FCSTD DOCUMENT  (FreeCAD 1.0R38641 +468 (Git))
Label: freecadCase
License: All rights reserved
LicenseURL: https://en.wikipedia.org/wiki/All_rights_reserved
objects: Sketcher::SketchObject×2, PartDesign::Body×1
note: 5 computed .brp shape members not serialized (recipe doc carries the construction recipe); baked Part::Feature solids carry a one-line shape summary decoded from their .brp

FEATURE [Sketcher::SketchObject] Sketch
  ArcFitTolerance = 1e-06
  FullyConstrained = false
  MakeInternals = false
  sketch-geometry (816):
    g0: LineSegment StartX=3.025 StartY=-2.525 StartZ=0 EndX=16.025 EndY=-2.525 EndZ=0
    g1: LineSegment StartX=3.025 StartY=-16.525 StartZ=0 EndX=16.025 EndY=-16.525 EndZ=0
    g2: LineSegment StartX=2.525 StartY=-3.025 StartZ=0 EndX=2.525 EndY=-16.025 EndZ=0
    g3: LineSegment StartX=16.525 StartY=-3.025 StartZ=0 EndX=16.525 EndY=-16.025 EndZ=0
    g4: ArcOfCircle CenterX=3.025 CenterY=-3.025 CenterZ=0 NormalX=0 NormalY=0 NormalZ=1 AngleXU=0 Radius=0.5 StartAngle=1.5708 EndAngle=3.14159
    g5: ArcOfCircle CenterX=16.025 CenterY=-3.025 CenterZ=0 NormalX=0 NormalY=0 NormalZ=1 AngleXU=0 Radius=0.5 StartAngle=0 EndAngle=1.5708
    g6: ArcOfCircle CenterX=3.025 CenterY=-16.025 CenterZ=0 NormalX=0 NormalY=0 NormalZ=1 AngleXU=0 Radius=0.5 StartAngle=3.14159 EndAngle=4.71239
    g7: ArcOfCircle CenterX=16.025 CenterY=-16.025 CenterZ=0 NormalX=0 NormalY=0 NormalZ=1 AngleXU=0 Radius=0.5 StartAngle=4.71239 EndAngle=6.28319
    g8: LineSegment StartX=22.075 StartY=-2.525 StartZ=0 EndX=35.075 EndY=-2.525 EndZ=0
    g9: LineSegment StartX=22.075 StartY=-16.525 StartZ=0 EndX=35.075 EndY=-16.525 EndZ=0
    g10: LineSegment StartX=21.575 StartY=-3.025 StartZ=0 EndX=21.575 EndY=-16.025 EndZ=0
    g11: LineSegment StartX=35.575 StartY=-3.025 StartZ=0 EndX=35.575 EndY=-16.025 EndZ=0
    g12: ArcOfCircle CenterX=22.075 CenterY=-3.025 CenterZ=0 NormalX=0 NormalY=0 NormalZ=1 AngleXU=0 Radius=0.5 StartAngle=1.5708 EndAngle=3.14159
    g13: ArcOfCircle CenterX=35.075 CenterY=-3.025 CenterZ=0 NormalX=0 NormalY=0 NormalZ=1 AngleXU=0 Radius=0.5 StartAngle=0 EndAngle=1.5708
    g14: ArcOfCircle CenterX=22.075 CenterY=-16.025 CenterZ=0 NormalX=0 NormalY=0 NormalZ=1 AngleXU=0 Radius=0.5 StartAngle=3.14159 EndAngle=4.71239
    g15: ArcOfCircle CenterX=35.075 CenterY=-16.025 CenterZ=0 NormalX=0 NormalY=0 NormalZ=1 AngleXU=0 Radius=0.5 StartAngle=4.71239 EndAngle=6.28319
    g16: LineSegment StartX=41.125 StartY=-2.525 StartZ=0 EndX=54.125 EndY=-2.525 EndZ=0
    g17: LineSegment StartX=41.125 StartY=-16.525 StartZ=0 EndX=54.125 EndY=-16.525 EndZ=0
    g18: LineSegment StartX=40.625 StartY=-3.025 StartZ=0 EndX=40.625 EndY=-16.025 EndZ=0
    g19: LineSegment StartX=54.625 StartY=-3.025 StartZ=0 EndX=54.625 EndY=-16.025 EndZ=0
    g20: ArcOfCircle CenterX=41.125 CenterY=-3.025 CenterZ=0 NormalX=0 NormalY=0 NormalZ=1 AngleXU=0 Radius=0.5 StartAngle=1.5708 EndAngle=3.14159
    g21: ArcOfCircle CenterX=54.125 CenterY=-3.025 CenterZ=0 NormalX=0 NormalY=0 NormalZ=1 AngleXU=0 Radius=0.5 StartAngle=0 EndAngle=1.5708
    g22: ArcOfCircle CenterX=41.125 CenterY=-16.025 CenterZ=0 NormalX=0 NormalY=0 NormalZ=1 AngleXU=0 Radius=0.5 StartAngle=3.14159 EndAngle=4.71239
    g23: ArcOfCircle CenterX=54.125 CenterY=-16.025 CenterZ=0 NormalX=0 NormalY=0 NormalZ=1 AngleXU=0 Radius=0.5 StartAngle=4.71239 EndAngle=6.28319
    g24: LineSegment StartX=60.175 StartY=-2.525 StartZ=0 EndX=73.175 EndY=-2.525 EndZ=0
    g25: LineSegment StartX=60.175 StartY=-16.525 StartZ=0 EndX=73.175 EndY=-16.525 EndZ=0
    g26: LineSegment StartX=59.675 StartY=-3.025 StartZ=0 EndX=59.675 EndY=-16.025 EndZ=0
    g27: LineSegment StartX=73.675 StartY=-3.025 StartZ=0 EndX=73.675 EndY=-16.025 EndZ=0
    g28: ArcOfCircle CenterX=60.175 CenterY=-3.025 CenterZ=0 NormalX=0 NormalY=0 NormalZ=1 AngleXU=0 Radius=0.5 StartAngle=1.5708 EndAngle=3.14159
    g29: ArcOfCircle CenterX=73.175 CenterY=-3.025 CenterZ=0 NormalX=0 NormalY=0 NormalZ=1 AngleXU=0 Radius=0.5 StartAngle=0 EndAngle=1.5708
    g30: ArcOfCircle CenterX=60.175 CenterY=-16.025 CenterZ=0 NormalX=0 NormalY=0 NormalZ=1 AngleXU=0 Radius=0.5 StartAngle=3.14159 EndAngle=4.71239
    g31: ArcOfCircle CenterX=73.175 CenterY=-16.025 CenterZ=0 NormalX=0 NormalY=0 NormalZ=1 AngleXU=0 Radius=0.5 StartAngle=4.71239 EndAngle=6.28319
    g32: LineSegment StartX=79.225 StartY=-2.525 StartZ=0 EndX=92.225 EndY=-2.525 EndZ=0
    g33: LineSegment StartX=79.225 StartY=-16.525 StartZ=0 EndX=92.225 EndY=-16.525 EndZ=0
    g34: LineSegment StartX=78.725 StartY=-3.025 StartZ=0 EndX=78.725 EndY=-16.025 EndZ=0
    g35: LineSegment StartX=92.725 StartY=-3.025 StartZ=0 EndX=92.725 EndY=-16.025 EndZ=0
    g36: ArcOfCircle CenterX=79.225 CenterY=-3.025 CenterZ=0 NormalX=0 NormalY=0 NormalZ=1 AngleXU=0 Radius=0.5 StartAngle=1.5708 EndAngle=3.14159
    g37: ArcOfCircle CenterX=92.225 CenterY=-3.025 CenterZ=0 NormalX=0 NormalY=0 NormalZ=1 AngleXU=0 Radius=0.5 StartAngle=0 EndAngle=1.5708
    g38: ArcOfCircle CenterX=79.225 CenterY=-16.025 CenterZ=0 NormalX=0 NormalY=0 NormalZ=1 AngleXU=0 Radius=0.5 StartAngle=3.14159 EndAngle=4.71239
    g39: ArcOfCircle CenterX=92.225 CenterY=-16.025 CenterZ=0 NormalX=0 NormalY=0 NormalZ=1 AngleXU=0 Radius=0.5 StartAngle=4.71239 EndAngle=6.28319
    g40: LineSegment StartX=98.275 StartY=-2.525 StartZ=0 EndX=111.275 EndY=-2.525 EndZ=0
    g41: LineSegment StartX=98.275 StartY=-16.525 StartZ=0 EndX=111.275 EndY=-16.525 EndZ=0
    g42: LineSegment StartX=97.775 StartY=-3.025 StartZ=0 EndX=97.775 EndY=-16.025 EndZ=0
    g43: LineSegment StartX=111.775 StartY=-3.025 StartZ=0 EndX=111.775 EndY=-16.025 EndZ=0
    g44: ArcOfCircle CenterX=98.275 CenterY=-3.025 CenterZ=0 NormalX=0 NormalY=0 NormalZ=1 AngleXU=0 Radius=0.5 StartAngle=1.5708 EndAngle=3.14159
    g45: ArcOfCircle CenterX=111.275 CenterY=-3.025 CenterZ=0 NormalX=0 NormalY=0 NormalZ=1 AngleXU=0 Radius=0.5 StartAngle=0 EndAngle=1.5708
    g46: ArcOfCircle CenterX=98.275 CenterY=-16.025 CenterZ=0 NormalX=0 NormalY=0 NormalZ=1 AngleXU=0 Radius=0.5 StartAngle=3.14159 EndAngle=4.71239
    g47: ArcOfCircle CenterX=111.275 CenterY=-16.025 CenterZ=0 NormalX=0 NormalY=0 NormalZ=1 AngleXU=0 Radius=0.5 StartAngle=4.71239 EndAngle=6.28319
    g48: LineSegment StartX=117.325 StartY=-2.525 StartZ=0 EndX=130.325 EndY=-2.525 EndZ=0
    g49: LineSegment StartX=117.325 StartY=-16.525 StartZ=0 EndX=130.325 EndY=-16.525 EndZ=0
    g50: LineSegment StartX=116.825 StartY=-3.025 StartZ=0 EndX=116.825 EndY=-16.025 EndZ=0
    g51: LineSegment StartX=130.825 StartY=-3.025 StartZ=0 EndX=130.825 EndY=-16.025 EndZ=0
    g52: ArcOfCircle CenterX=117.325 CenterY=-3.025 CenterZ=0 NormalX=0 NormalY=0 NormalZ=1 AngleXU=0 Radius=0.5 StartAngle=1.5708 EndAngle=3.14159
    g53: ArcOfCircle CenterX=130.325 CenterY=-3.025 CenterZ=0 NormalX=0 NormalY=0 NormalZ=1 AngleXU=0 Radius=0.5 StartAngle=0 EndAngle=1.5708
    g54: ArcOfCircle CenterX=117.325 CenterY=-16.025 CenterZ=0 NormalX=0 NormalY=0 NormalZ=1 AngleXU=0 Radius=0.5 StartAngle=3.14159 EndAngle=4.71239
    g55: ArcOfCircle CenterX=130.325 CenterY=-16.025 CenterZ=0 NormalX=0 NormalY=0 NormalZ=1 AngleXU=0 Radius=0.5 StartAngle=4.71239 EndAngle=6.28319
    g56: LineSegment StartX=136.375 StartY=-2.525 StartZ=0 EndX=149.375 EndY=-2.525 EndZ=0
    g57: LineSegment StartX=136.375 StartY=-16.525 StartZ=0 EndX=149.375 EndY=-16.525 EndZ=0
    g58: LineSegment StartX=135.875 StartY=-3.025 StartZ=0 EndX=135.875 EndY=-16.025 EndZ=0
    g59: LineSegment StartX=149.875 StartY=-3.025 StartZ=0 EndX=149.875 EndY=-16.025 EndZ=0
    g60: ArcOfCircle CenterX=136.375 CenterY=-3.025 CenterZ=0 NormalX=0 NormalY=0 NormalZ=1 AngleXU=0 Radius=0.5 StartAngle=1.5708 EndAngle=3.14159
    g61: ArcOfCircle CenterX=149.375 CenterY=-3.025 CenterZ=0 NormalX=0 NormalY=0 NormalZ=1 AngleXU=0 Radius=0.5 StartAngle=0 EndAngle=1.5708
    g62: ArcOfCircle CenterX=136.375 CenterY=-16.025 CenterZ=0 NormalX=0 NormalY=0 NormalZ=1 AngleXU=0 Radius=0.5 StartAngle=3.14159 EndAngle=4.71239
    g63: ArcOfCircle CenterX=149.375 CenterY=-16.025 CenterZ=0 NormalX=0 NormalY=0 NormalZ=1 AngleXU=0 Radius=0.5 StartAngle=4.71239 EndAngle=6.28319
    g64: LineSegment StartX=155.425 StartY=-2.525 StartZ=0 EndX=168.425 EndY=-2.525 EndZ=0
    g65: LineSegment StartX=155.425 StartY=-16.525 StartZ=0 EndX=168.425 EndY=-16.525 EndZ=0
    g66: LineSegment StartX=154.925 StartY=-3.025 StartZ=0 EndX=154.925 EndY=-16.025 EndZ=0
    g67: LineSegment StartX=168.925 StartY=-3.025 StartZ=0 EndX=168.925 EndY=-16.025 EndZ=0
    g68: ArcOfCircle CenterX=155.425 CenterY=-3.025 CenterZ=0 NormalX=0 NormalY=0 NormalZ=1 AngleXU=0 Radius=0.5 StartAngle=1.5708 EndAngle=3.14159
    g69: ArcOfCircle CenterX=168.425 CenterY=-3.025 CenterZ=0 NormalX=0 NormalY=0 NormalZ=1 AngleXU=0 Radius=0.5 StartAngle=0 EndAngle=1.5708
    g70: ArcOfCircle CenterX=155.425 CenterY=-16.025 CenterZ=0 NormalX=0 NormalY=0 NormalZ=1 AngleXU=0 Radius=0.5 StartAngle=3.14159 EndAngle=4.71239
    g71: ArcOfCircle CenterX=168.425 CenterY=-16.025 CenterZ=0 NormalX=0 NormalY=0 NormalZ=1 AngleXU=0 Radius=0.5 StartAngle=4.71239 EndAngle=6.28319
    g72: LineSegment StartX=174.475 StartY=-2.525 StartZ=0 EndX=187.475 EndY=-2.525 EndZ=0
    g73: LineSegment StartX=174.475 StartY=-16.525 StartZ=0 EndX=187.475 EndY=-16.525 EndZ=0
    g74: LineSegment StartX=173.975 StartY=-3.025 StartZ=0 EndX=173.975 EndY=-16.025 EndZ=0
    g75: LineSegment StartX=187.975 StartY=-3.025 StartZ=0 EndX=187.975 EndY=-16.025 EndZ=0
    g76: ArcOfCircle CenterX=174.475 CenterY=-3.025 CenterZ=0 NormalX=0 NormalY=0 NormalZ=1 AngleXU=0 Radius=0.5 StartAngle=1.5708 EndAngle=3.14159
    g77: ArcOfCircle CenterX=187.475 CenterY=-3.025 CenterZ=0 NormalX=0 NormalY=0 NormalZ=1 AngleXU=0 Radius=0.5 StartAngle=0 EndAngle=1.5708
    g78: ArcOfCircle CenterX=174.475 CenterY=-16.025 CenterZ=0 NormalX=0 NormalY=0 NormalZ=1 AngleXU=0 Radius=0.5 StartAngle=3.14159 EndAngle=4.71239
    g79: ArcOfCircle CenterX=187.475 CenterY=-16.025 CenterZ=0 NormalX=0 NormalY=0 NormalZ=1 AngleXU=0 Radius=0.5 StartAngle=4.71239 EndAngle=6.28319
    g80: LineSegment StartX=193.525 StartY=-2.525 StartZ=0 EndX=206.525 EndY=-2.525 EndZ=0
    g81: LineSegment StartX=193.525 StartY=-16.525 StartZ=0 EndX=206.525 EndY=-16.525 EndZ=0
    g82: LineSegment StartX=193.025 StartY=-3.025 StartZ=0 EndX=193.025 EndY=-16.025 EndZ=0
    g83: LineSegment StartX=207.025 StartY=-3.025 StartZ=0 EndX=207.025 EndY=-16.025 EndZ=0
    g84: ArcOfCircle CenterX=193.525 CenterY=-3.025 CenterZ=0 NormalX=0 NormalY=0 NormalZ=1 AngleXU=0 Radius=0.5 StartAngle=1.5708 EndAngle=3.14159
    g85: ArcOfCircle CenterX=206.525 CenterY=-3.025 CenterZ=0 NormalX=0 NormalY=0 NormalZ=1 AngleXU=0 Radius=0.5 StartAngle=0 EndAngle=1.5708
    g86: ArcOfCircle CenterX=193.525 CenterY=-16.025 CenterZ=0 NormalX=0 NormalY=0 NormalZ=1 AngleXU=0 Radius=0.5 StartAngle=3.14159 EndAngle=4.71239
    g87: ArcOfCircle CenterX=206.525 CenterY=-16.025 CenterZ=0 NormalX=0 NormalY=0 NormalZ=1 AngleXU=0 Radius=0.5 StartAngle=4.71239 EndAngle=6.28319
    g88: LineSegment StartX=212.575 StartY=-2.525 StartZ=0 EndX=225.575 EndY=-2.525 EndZ=0
    g89: LineSegment StartX=212.575 StartY=-16.525 StartZ=0 EndX=225.575 EndY=-16.525 EndZ=0
    g90: LineSegment StartX=212.075 StartY=-3.025 StartZ=0 EndX=212.075 EndY=-16.025 EndZ=0
    g91: LineSegment StartX=226.075 StartY=-3.025 StartZ=0 EndX=226.075 EndY=-16.025 EndZ=0
    g92: ArcOfCircle CenterX=212.575 CenterY=-3.025 CenterZ=0 NormalX=0 NormalY=0 NormalZ=1 AngleXU=0 Radius=0.5 StartAngle=1.5708 EndAngle=3.14159
    g93: ArcOfCircle CenterX=225.575 CenterY=-3.025 CenterZ=0 NormalX=0 NormalY=0 NormalZ=1 AngleXU=0 Radius=0.5 StartAngle=0 EndAngle=1.5708
    g94: ArcOfCircle CenterX=212.575 CenterY=-16.025 CenterZ=0 NormalX=0 NormalY=0 NormalZ=1 AngleXU=0 Radius=0.5 StartAngle=3.14159 EndAngle=4.71239
    g95: ArcOfCircle CenterX=225.575 CenterY=-16.025 CenterZ=0 NormalX=0 NormalY=0 NormalZ=1 AngleXU=0 Radius=0.5 StartAngle=4.71239 EndAngle=6.28319
    g96: LineSegment StartX=231.625 StartY=-2.525 StartZ=0 EndX=244.625 EndY=-2.525 EndZ=0
    g97: LineSegment StartX=231.625 StartY=-16.525 StartZ=0 EndX=244.625 EndY=-16.525 EndZ=0
    g98: LineSegment StartX=231.125 StartY=-3.025 StartZ=0 EndX=231.125 EndY=-16.025 EndZ=0
    g99: LineSegment StartX=245.125 StartY=-3.025 StartZ=0 EndX=245.125 EndY=-16.025 EndZ=0
    g100: ArcOfCircle CenterX=231.625 CenterY=-3.025 CenterZ=0 NormalX=0 NormalY=0 NormalZ=1 AngleXU=0 Radius=0.5 StartAngle=1.5708 EndAngle=3.14159
    g101: ArcOfCircle CenterX=244.625 CenterY=-3.025 CenterZ=0 NormalX=0 NormalY=0 NormalZ=1 AngleXU=0 Radius=0.5 StartAngle=0 EndAngle=1.5708
    g102: ArcOfCircle CenterX=231.625 CenterY=-16.025 CenterZ=0 NormalX=0 NormalY=0 NormalZ=1 AngleXU=0 Radius=0.5 StartAngle=3.14159 EndAngle=4.71239
    g103: ArcOfCircle CenterX=244.625 CenterY=-16.025 CenterZ=0 NormalX=0 NormalY=0 NormalZ=1 AngleXU=0 Radius=0.5 StartAngle=4.71239 EndAngle=6.28319
    g104: LineSegment StartX=269.725 StartY=-2.525 StartZ=0 EndX=282.725 EndY=-2.525 EndZ=0
    g105: LineSegment StartX=269.725 StartY=-16.525 StartZ=0 EndX=282.725 EndY=-16.525 EndZ=0
    g106: LineSegment StartX=269.225 StartY=-3.025 StartZ=0 EndX=269.225 EndY=-16.025 EndZ=0
    g107: LineSegment StartX=283.225 StartY=-3.025 StartZ=0 EndX=283.225 EndY=-16.025 EndZ=0
    g108: ArcOfCircle CenterX=269.725 CenterY=-3.025 CenterZ=0 NormalX=0 NormalY=0 NormalZ=1 AngleXU=0 Radius=0.5 StartAngle=1.5708 EndAngle=3.14159
    g109: ArcOfCircle CenterX=282.725 CenterY=-3.025 CenterZ=0 NormalX=0 NormalY=0 NormalZ=1 AngleXU=0 Radius=0.5 StartAngle=0 EndAngle=1.5708
    g110: ArcOfCircle CenterX=269.725 CenterY=-16.025 CenterZ=0 NormalX=0 NormalY=0 NormalZ=1 AngleXU=0 Radius=0.5 StartAngle=3.14159 EndAngle=4.71239
    g111: ArcOfCircle CenterX=282.725 CenterY=-16.025 CenterZ=0 NormalX=0 NormalY=0 NormalZ=1 AngleXU=0 Radius=0.5 StartAngle=4.71239 EndAngle=6.28319
    g112: LineSegment StartX=288.775 StartY=-2.525 StartZ=0 EndX=301.775 EndY=-2.525 EndZ=0
    g113: LineSegment StartX=288.775 StartY=-16.525 StartZ=0 EndX=301.775 EndY=-16.525 EndZ=0
    g114: LineSegment StartX=288.275 StartY=-3.025 StartZ=0 EndX=288.275 EndY=-16.025 EndZ=0
    g115: LineSegment StartX=302.275 StartY=-3.025 StartZ=0 EndX=302.275 EndY=-16.025 EndZ=0
    g116: ArcOfCircle CenterX=288.775 CenterY=-3.025 CenterZ=0 NormalX=0 NormalY=0 NormalZ=1 AngleXU=0 Radius=0.5 StartAngle=1.5708 EndAngle=3.14159
    g117: ArcOfCircle CenterX=301.775 CenterY=-3.025 CenterZ=0 NormalX=0 NormalY=0 NormalZ=1 AngleXU=0 Radius=0.5 StartAngle=0 EndAngle=1.5708
    g118: ArcOfCircle CenterX=288.775 CenterY=-16.025 CenterZ=0 NormalX=0 NormalY=0 NormalZ=1 AngleXU=0 Radius=0.5 StartAngle=3.14159 EndAngle=4.71239
    g119: ArcOfCircle CenterX=301.775 CenterY=-16.025 CenterZ=0 NormalX=0 NormalY=0 NormalZ=1 AngleXU=0 Radius=0.5 StartAngle=4.71239 EndAngle=6.28319
    g120: LineSegment StartX=336.4 StartY=-2.525 StartZ=0 EndX=349.4 EndY=-2.525 EndZ=0
    g121: LineSegment StartX=336.4 StartY=-16.525 StartZ=0 EndX=349.4 EndY=-16.525 EndZ=0
    g122: LineSegment StartX=335.9 StartY=-3.025 StartZ=0 EndX=335.9 EndY=-16.025 EndZ=0
    g123: LineSegment StartX=349.9 StartY=-3.025 StartZ=0 EndX=349.9 EndY=-16.025 EndZ=0
    g124: ArcOfCircle CenterX=336.4 CenterY=-3.025 CenterZ=0 NormalX=0 NormalY=0 NormalZ=1 AngleXU=0 Radius=0.5 StartAngle=1.5708 EndAngle=3.14159
    g125: ArcOfCircle CenterX=349.4 CenterY=-3.025 CenterZ=0 NormalX=0 NormalY=0 NormalZ=1 AngleXU=0 Radius=0.5 StartAngle=0 EndAngle=1.5708
    g126: ArcOfCircle CenterX=336.4 CenterY=-16.025 CenterZ=0 NormalX=0 NormalY=0 NormalZ=1 AngleXU=0 Radius=0.5 StartAngle=3.14159 EndAngle=4.71239
    g127: ArcOfCircle CenterX=349.4 CenterY=-16.025 CenterZ=0 NormalX=0 NormalY=0 NormalZ=1 AngleXU=0 Radius=0.5 StartAngle=4.71239 EndAngle=6.28319
    g128: LineSegment StartX=3.025 StartY=-31.1 StartZ=0 EndX=16.025 EndY=-31.1 EndZ=0
    g129: LineSegment StartX=3.025 StartY=-45.1 StartZ=0 EndX=16.025 EndY=-45.1 EndZ=0
    g130: LineSegment StartX=2.525 StartY=-31.6 StartZ=0 EndX=2.525 EndY=-44.6 EndZ=0
    g131: LineSegment StartX=16.525 StartY=-31.6 StartZ=0 EndX=16.525 EndY=-44.6 EndZ=0
    g132: ArcOfCircle CenterX=3.025 CenterY=-31.6 CenterZ=0 NormalX=0 NormalY=0 NormalZ=1 AngleXU=0 Radius=0.5 StartAngle=1.5708 EndAngle=3.14159
    g133: ArcOfCircle CenterX=16.025 CenterY=-31.6 CenterZ=0 NormalX=0 NormalY=0 NormalZ=1 AngleXU=0 Radius=0.5 StartAngle=0 EndAngle=1.5708
    g134: ArcOfCircle CenterX=3.025 CenterY=-44.6 CenterZ=0 NormalX=0 NormalY=0 NormalZ=1 AngleXU=0 Radius=0.5 StartAngle=3.14159 EndAngle=4.71239
    g135: ArcOfCircle CenterX=16.025 CenterY=-44.6 CenterZ=0 NormalX=0 NormalY=0 NormalZ=1 AngleXU=0 Radius=0.5 StartAngle=4.71239 EndAngle=6.28319
    g136: LineSegment StartX=22.075 StartY=-31.1 StartZ=0 EndX=35.075 EndY=-31.1 EndZ=0
    g137: LineSegment StartX=22.075 StartY=-45.1 StartZ=0 EndX=35.075 EndY=-45.1 EndZ=0
    g138: LineSegment StartX=21.575 StartY=-31.6 StartZ=0 EndX=21.575 EndY=-44.6 EndZ=0
    g139: LineSegment StartX=35.575 StartY=-31.6 StartZ=0 EndX=35.575 EndY=-44.6 EndZ=0
    g140: ArcOfCircle CenterX=22.075 CenterY=-31.6 CenterZ=0 NormalX=0 NormalY=0 NormalZ=1 AngleXU=0 Radius=0.5 StartAngle=1.5708 EndAngle=3.14159
    g141: ArcOfCircle CenterX=35.075 CenterY=-31.6 CenterZ=0 NormalX=0 NormalY=0 NormalZ=1 AngleXU=0 Radius=0.5 StartAngle=0 EndAngle=1.5708
    g142: ArcOfCircle CenterX=22.075 CenterY=-44.6 CenterZ=0 NormalX=0 NormalY=0 NormalZ=1 AngleXU=0 Radius=0.5 StartAngle=3.14159 EndAngle=4.71239
    g143: ArcOfCircle CenterX=35.075 CenterY=-44.6 CenterZ=0 NormalX=0 NormalY=0 NormalZ=1 AngleXU=0 Radius=0.5 StartAngle=4.71239 EndAngle=6.28319
    g144: LineSegment StartX=41.125 StartY=-31.1 StartZ=0 EndX=54.125 EndY=-31.1 EndZ=0
    g145: LineSegment StartX=41.125 StartY=-45.1 StartZ=0 EndX=54.125 EndY=-45.1 EndZ=0
    g146: LineSegment StartX=40.625 StartY=-31.6 StartZ=0 EndX=40.625 EndY=-44.6 EndZ=0
    g147: LineSegment StartX=54.625 StartY=-31.6 StartZ=0 EndX=54.625 EndY=-44.6 EndZ=0
    g148: ArcOfCircle CenterX=41.125 CenterY=-31.6 CenterZ=0 NormalX=0 NormalY=0 NormalZ=1 AngleXU=0 Radius=0.5 StartAngle=1.5708 EndAngle=3.14159
    g149: ArcOfCircle CenterX=54.125 CenterY=-31.6 CenterZ=0 NormalX=0 NormalY=0 NormalZ=1 AngleXU=0 Radius=0.5 StartAngle=0 EndAngle=1.5708
    g150: ArcOfCircle CenterX=41.125 CenterY=-44.6 CenterZ=0 NormalX=0 NormalY=0 NormalZ=1 AngleXU=0 Radius=0.5 StartAngle=3.14159 EndAngle=4.71239
    g151: ArcOfCircle CenterX=54.125 CenterY=-44.6 CenterZ=0 NormalX=0 NormalY=0 NormalZ=1 AngleXU=0 Radius=0.5 StartAngle=4.71239 EndAngle=6.28319
    g152: LineSegment StartX=60.175 StartY=-31.1 StartZ=0 EndX=73.175 EndY=-31.1 EndZ=0
    g153: LineSegment StartX=60.175 StartY=-45.1 StartZ=0 EndX=73.175 EndY=-45.1 EndZ=0
    g154: LineSegment StartX=59.675 StartY=-31.6 StartZ=0 EndX=59.675 EndY=-44.6 EndZ=0
    g155: LineSegment StartX=73.675 StartY=-31.6 StartZ=0 EndX=73.675 EndY=-44.6 EndZ=0
    g156: ArcOfCircle CenterX=60.175 CenterY=-31.6 CenterZ=0 NormalX=0 NormalY=0 NormalZ=1 AngleXU=0 Radius=0.5 StartAngle=1.5708 EndAngle=3.14159
    g157: ArcOfCircle CenterX=73.175 CenterY=-31.6 CenterZ=0 NormalX=0 NormalY=0 NormalZ=1 AngleXU=0 Radius=0.5 StartAngle=0 EndAngle=1.5708
    g158: ArcOfCircle CenterX=60.175 CenterY=-44.6 CenterZ=0 NormalX=0 NormalY=0 NormalZ=1 AngleXU=0 Radius=0.5 StartAngle=3.14159 EndAngle=4.71239
    g159: ArcOfCircle CenterX=73.175 CenterY=-44.6 CenterZ=0 NormalX=0 NormalY=0 NormalZ=1 AngleXU=0 Radius=0.5 StartAngle=4.71239 EndAngle=6.28319
    g160: LineSegment StartX=79.225 StartY=-31.1 StartZ=0 EndX=92.225 EndY=-31.1 EndZ=0
    g161: LineSegment StartX=79.225 StartY=-45.1 StartZ=0 EndX=92.225 EndY=-45.1 EndZ=0
    g162: LineSegment StartX=78.725 StartY=-31.6 StartZ=0 EndX=78.725 EndY=-44.6 EndZ=0
    g163: LineSegment StartX=92.725 StartY=-31.6 StartZ=0 EndX=92.725 EndY=-44.6 EndZ=0
    g164: ArcOfCircle CenterX=79.225 CenterY=-31.6 CenterZ=0 NormalX=0 NormalY=0 NormalZ=1 AngleXU=0 Radius=0.5 StartAngle=1.5708 EndAngle=3.14159
    g165: ArcOfCircle CenterX=92.225 CenterY=-31.6 CenterZ=0 NormalX=0 NormalY=0 NormalZ=1 AngleXU=0 Radius=0.5 StartAngle=0 EndAngle=1.5708
    g166: ArcOfCircle CenterX=79.225 CenterY=-44.6 CenterZ=0 NormalX=0 NormalY=0 NormalZ=1 AngleXU=0 Radius=0.5 StartAngle=3.14159 EndAngle=4.71239
    g167: ArcOfCircle CenterX=92.225 CenterY=-44.6 CenterZ=0 NormalX=0 NormalY=0 NormalZ=1 AngleXU=0 Radius=0.5 StartAngle=4.71239 EndAngle=6.28319
    g168: LineSegment StartX=98.275 StartY=-31.1 StartZ=0 EndX=111.275 EndY=-31.1 EndZ=0
    g169: LineSegment StartX=98.275 StartY=-45.1 StartZ=0 EndX=111.275 EndY=-45.1 EndZ=0
    g170: LineSegment StartX=97.775 StartY=-31.6 StartZ=0 EndX=97.775 EndY=-44.6 EndZ=0
    g171: LineSegment StartX=111.775 StartY=-31.6 StartZ=0 EndX=111.775 EndY=-44.6 EndZ=0
    g172: ArcOfCircle CenterX=98.275 CenterY=-31.6 CenterZ=0 NormalX=0 NormalY=0 NormalZ=1 AngleXU=0 Radius=0.5 StartAngle=1.5708 EndAngle=3.14159
    g173: ArcOfCircle CenterX=111.275 CenterY=-31.6 CenterZ=0 NormalX=0 NormalY=0 NormalZ=1 AngleXU=0 Radius=0.5 StartAngle=0 EndAngle=1.5708
    g174: ArcOfCircle CenterX=98.275 CenterY=-44.6 CenterZ=0 NormalX=0 NormalY=0 NormalZ=1 AngleXU=0 Radius=0.5 StartAngle=3.14159 EndAngle=4.71239
    g175: ArcOfCircle CenterX=111.275 CenterY=-44.6 CenterZ=0 NormalX=0 NormalY=0 NormalZ=1 AngleXU=0 Radius=0.5 StartAngle=4.71239 EndAngle=6.28319
    g176: LineSegment StartX=117.325 StartY=-31.1 StartZ=0 EndX=130.325 EndY=-31.1 EndZ=0
    g177: LineSegment StartX=117.325 StartY=-45.1 StartZ=0 EndX=130.325 EndY=-45.1 EndZ=0
    g178: LineSegment StartX=116.825 StartY=-31.6 StartZ=0 EndX=116.825 EndY=-44.6 EndZ=0
    g179: LineSegment StartX=130.825 StartY=-31.6 StartZ=0 EndX=130.825 EndY=-44.6 EndZ=0
    g180: ArcOfCircle CenterX=117.325 CenterY=-31.6 CenterZ=0 NormalX=0 NormalY=0 NormalZ=1 AngleXU=0 Radius=0.5 StartAngle=1.5708 EndAngle=3.14159
    g181: ArcOfCircle CenterX=130.325 CenterY=-31.6 CenterZ=0 NormalX=0 NormalY=0 NormalZ=1 AngleXU=0 Radius=0.5 StartAngle=0 EndAngle=1.5708
    g182: ArcOfCircle CenterX=117.325 CenterY=-44.6 CenterZ=0 NormalX=0 NormalY=0 NormalZ=1 AngleXU=0 Radius=0.5 StartAngle=3.14159 EndAngle=4.71239
    g183: ArcOfCircle CenterX=130.325 CenterY=-44.6 CenterZ=0 NormalX=0 NormalY=0 NormalZ=1 AngleXU=0 Radius=0.5 StartAngle=4.71239 EndAngle=6.28319
    g184: LineSegment StartX=136.375 StartY=-31.1 StartZ=0 EndX=149.375 EndY=-31.1 EndZ=0
    g185: LineSegment StartX=136.375 StartY=-45.1 StartZ=0 EndX=149.375 EndY=-45.1 EndZ=0
    g186: LineSegment StartX=135.875 StartY=-31.6 StartZ=0 EndX=135.875 EndY=-44.6 EndZ=0
    g187: LineSegment StartX=149.875 StartY=-31.6 StartZ=0 EndX=149.875 EndY=-44.6 EndZ=0
    g188: ArcOfCircle CenterX=136.375 CenterY=-31.6 CenterZ=0 NormalX=0 NormalY=0 NormalZ=1 AngleXU=0 Radius=0.5 StartAngle=1.5708 EndAngle=3.14159
    g189: ArcOfCircle CenterX=149.375 CenterY=-31.6 CenterZ=0 NormalX=0 NormalY=0 NormalZ=1 AngleXU=0 Radius=0.5 StartAngle=0 EndAngle=1.5708
    g190: ArcOfCircle CenterX=136.375 CenterY=-44.6 CenterZ=0 NormalX=0 NormalY=0 NormalZ=1 AngleXU=0 Radius=0.5 StartAngle=3.14159 EndAngle=4.71239
    g191: ArcOfCircle CenterX=149.375 CenterY=-44.6 CenterZ=0 NormalX=0 NormalY=0 NormalZ=1 AngleXU=0 Radius=0.5 StartAngle=4.71239 EndAngle=6.28319
    g192: LineSegment StartX=155.425 StartY=-31.1 StartZ=0 EndX=168.425 EndY=-31.1 EndZ=0
    g193: LineSegment StartX=155.425 StartY=-45.1 StartZ=0 EndX=168.425 EndY=-45.1 EndZ=0
    g194: LineSegment StartX=154.925 StartY=-31.6 StartZ=0 EndX=154.925 EndY=-44.6 EndZ=0
    g195: LineSegment StartX=168.925 StartY=-31.6 StartZ=0 EndX=168.925 EndY=-44.6 EndZ=0
    g196: ArcOfCircle CenterX=155.425 CenterY=-31.6 CenterZ=0 NormalX=0 NormalY=0 NormalZ=1 AngleXU=0 Radius=0.5 StartAngle=1.5708 EndAngle=3.14159
    g197: ArcOfCircle CenterX=168.425 CenterY=-31.6 CenterZ=0 NormalX=0 NormalY=0 NormalZ=1 AngleXU=0 Radius=0.5 StartAngle=0 EndAngle=1.5708
    g198: ArcOfCircle CenterX=155.425 CenterY=-44.6 CenterZ=0 NormalX=0 NormalY=0 NormalZ=1 AngleXU=0 Radius=0.5 StartAngle=3.14159 EndAngle=4.71239
    g199: ArcOfCircle CenterX=168.425 CenterY=-44.6 CenterZ=0 NormalX=0 NormalY=0 NormalZ=1 AngleXU=0 Radius=0.5 StartAngle=4.71239 EndAngle=6.28319
    g200: LineSegment StartX=174.475 StartY=-31.1 StartZ=0 EndX=187.475 EndY=-31.1 EndZ=0
    g201: LineSegment StartX=174.475 StartY=-45.1 StartZ=0 EndX=187.475 EndY=-45.1 EndZ=0
    g202: LineSegment StartX=173.975 StartY=-31.6 StartZ=0 EndX=173.975 EndY=-44.6 EndZ=0
    g203: LineSegment StartX=187.975 StartY=-31.6 StartZ=0 EndX=187.975 EndY=-44.6 EndZ=0
    g204: ArcOfCircle CenterX=174.475 CenterY=-31.6 CenterZ=0 NormalX=0 NormalY=0 NormalZ=1 AngleXU=0 Radius=0.5 StartAngle=1.5708 EndAngle=3.14159
    g205: ArcOfCircle CenterX=187.475 CenterY=-31.6 CenterZ=0 NormalX=0 NormalY=0 NormalZ=1 AngleXU=0 Radius=0.5 StartAngle=0 EndAngle=1.5708
    g206: ArcOfCircle CenterX=174.475 CenterY=-44.6 CenterZ=0 NormalX=0 NormalY=0 NormalZ=1 AngleXU=0 Radius=0.5 StartAngle=3.14159 EndAngle=4.71239
    g207: ArcOfCircle CenterX=187.475 CenterY=-44.6 CenterZ=0 NormalX=0 NormalY=0 NormalZ=1 AngleXU=0 Radius=0.5 StartAngle=4.71239 EndAngle=6.28319
    g208: LineSegment StartX=193.525 StartY=-31.1 StartZ=0 EndX=206.525 EndY=-31.1 EndZ=0
    g209: LineSegment StartX=193.525 StartY=-45.1 StartZ=0 EndX=206.525 EndY=-45.1 EndZ=0
    g210: LineSegment StartX=193.025 StartY=-31.6 StartZ=0 EndX=193.025 EndY=-44.6 EndZ=0
    g211: LineSegment StartX=207.025 StartY=-31.6 StartZ=0 EndX=207.025 EndY=-44.6 EndZ=0
    g212: ArcOfCircle CenterX=193.525 CenterY=-31.6 CenterZ=0 NormalX=0 NormalY=0 NormalZ=1 AngleXU=0 Radius=0.5 StartAngle=1.5708 EndAngle=3.14159
    g213: ArcOfCircle CenterX=206.525 CenterY=-31.6 CenterZ=0 NormalX=0 NormalY=0 NormalZ=1 AngleXU=0 Radius=0.5 StartAngle=0 EndAngle=1.5708
    g214: ArcOfCircle CenterX=193.525 CenterY=-44.6 CenterZ=0 NormalX=0 NormalY=0 NormalZ=1 AngleXU=0 Radius=0.5 StartAngle=3.14159 EndAngle=4.71239
    g215: ArcOfCircle CenterX=206.525 CenterY=-44.6 CenterZ=0 NormalX=0 NormalY=0 NormalZ=1 AngleXU=0 Radius=0.5 StartAngle=4.71239 EndAngle=6.28319
    g216: LineSegment StartX=212.575 StartY=-31.1 StartZ=0 EndX=225.575 EndY=-31.1 EndZ=0
    g217: LineSegment StartX=212.575 StartY=-45.1 StartZ=0 EndX=225.575 EndY=-45.1 EndZ=0
    g218: LineSegment StartX=212.075 StartY=-31.6 StartZ=0 EndX=212.075 EndY=-44.6 EndZ=0
    g219: LineSegment StartX=226.075 StartY=-31.6 StartZ=0 EndX=226.075 EndY=-44.6 EndZ=0
    g220: ArcOfCircle CenterX=212.575 CenterY=-31.6 CenterZ=0 NormalX=0 NormalY=0 NormalZ=1 AngleXU=0 Radius=0.5 StartAngle=1.5708 EndAngle=3.14159
    g221: ArcOfCircle CenterX=225.575 CenterY=-31.6 CenterZ=0 NormalX=0 NormalY=0 NormalZ=1 AngleXU=0 Radius=0.5 StartAngle=0 EndAngle=1.5708
    g222: ArcOfCircle CenterX=212.575 CenterY=-44.6 CenterZ=0 NormalX=0 NormalY=0 NormalZ=1 AngleXU=0 Radius=0.5 StartAngle=3.14159 EndAngle=4.71239
    g223: ArcOfCircle CenterX=225.575 CenterY=-44.6 CenterZ=0 NormalX=0 NormalY=0 NormalZ=1 AngleXU=0 Radius=0.5 StartAngle=4.71239 EndAngle=6.28319
    g224: LineSegment StartX=231.625 StartY=-31.1 StartZ=0 EndX=244.625 EndY=-31.1 EndZ=0
    g225: LineSegment StartX=231.625 StartY=-45.1 StartZ=0 EndX=244.625 EndY=-45.1 EndZ=0
    g226: LineSegment StartX=231.125 StartY=-31.6 StartZ=0 EndX=231.125 EndY=-44.6 EndZ=0
    g227: LineSegment StartX=245.125 StartY=-31.6 StartZ=0 EndX=245.125 EndY=-44.6 EndZ=0
    g228: ArcOfCircle CenterX=231.625 CenterY=-31.6 CenterZ=0 NormalX=0 NormalY=0 NormalZ=1 AngleXU=0 Radius=0.5 StartAngle=1.5708 EndAngle=3.14159
    g229: ArcOfCircle CenterX=244.625 CenterY=-31.6 CenterZ=0 NormalX=0 NormalY=0 NormalZ=1 AngleXU=0 Radius=0.5 StartAngle=0 EndAngle=1.5708
    g230: ArcOfCircle CenterX=231.625 CenterY=-44.6 CenterZ=0 NormalX=0 NormalY=0 NormalZ=1 AngleXU=0 Radius=0.5 StartAngle=3.14159 EndAngle=4.71239
    g231: ArcOfCircle CenterX=244.625 CenterY=-44.6 CenterZ=0 NormalX=0 NormalY=0 NormalZ=1 AngleXU=0 Radius=0.5 StartAngle=4.71239 EndAngle=6.28319
    g232: LineSegment StartX=250.675 StartY=-31.1 StartZ=0 EndX=263.675 EndY=-31.1 EndZ=0
    g233: LineSegment StartX=250.675 StartY=-45.1 StartZ=0 EndX=263.675 EndY=-45.1 EndZ=0
    g234: LineSegment StartX=250.175 StartY=-31.6 StartZ=0 EndX=250.175 EndY=-44.6 EndZ=0
    g235: LineSegment StartX=264.175 StartY=-31.6 StartZ=0 EndX=264.175 EndY=-44.6 EndZ=0
    g236: ArcOfCircle CenterX=250.675 CenterY=-31.6 CenterZ=0 NormalX=0 NormalY=0 NormalZ=1 AngleXU=0 Radius=0.5 StartAngle=1.5708 EndAngle=3.14159
    g237: ArcOfCircle CenterX=263.675 CenterY=-31.6 CenterZ=0 NormalX=0 NormalY=0 NormalZ=1 AngleXU=0 Radius=0.5 StartAngle=0 EndAngle=1.5708
    g238: ArcOfCircle CenterX=250.675 CenterY=-44.6 CenterZ=0 NormalX=0 NormalY=0 NormalZ=1 AngleXU=0 Radius=0.5 StartAngle=3.14159 EndAngle=4.71239
    g239: ArcOfCircle CenterX=263.675 CenterY=-44.6 CenterZ=0 NormalX=0 NormalY=0 NormalZ=1 AngleXU=0 Radius=0.5 StartAngle=4.71239 EndAngle=6.28319
    g240: LineSegment StartX=269.725 StartY=-31.1 StartZ=0 EndX=282.725 EndY=-31.1 EndZ=0
    g241: LineSegment StartX=269.725 StartY=-45.1 StartZ=0 EndX=282.725 EndY=-45.1 EndZ=0
    g242: LineSegment StartX=269.225 StartY=-31.6 StartZ=0 EndX=269.225 EndY=-44.6 EndZ=0
    g243: LineSegment StartX=283.225 StartY=-31.6 StartZ=0 EndX=283.225 EndY=-44.6 EndZ=0
    g244: ArcOfCircle CenterX=269.725 CenterY=-31.6 CenterZ=0 NormalX=0 NormalY=0 NormalZ=1 AngleXU=0 Radius=0.5 StartAngle=1.5708 EndAngle=3.14159
    g245: ArcOfCircle CenterX=282.725 CenterY=-31.6 CenterZ=0 NormalX=0 NormalY=0 NormalZ=1 AngleXU=0 Radius=0.5 StartAngle=0 EndAngle=1.5708
    g246: ArcOfCircle CenterX=269.725 CenterY=-44.6 CenterZ=0 NormalX=0 NormalY=0 NormalZ=1 AngleXU=0 Radius=0.5 StartAngle=3.14159 EndAngle=4.71239
    g247: ArcOfCircle CenterX=282.725 CenterY=-44.6 CenterZ=0 NormalX=0 NormalY=0 NormalZ=1 AngleXU=0 Radius=0.5 StartAngle=4.71239 EndAngle=6.28319
    g248: LineSegment StartX=288.775 StartY=-31.1 StartZ=0 EndX=301.775 EndY=-31.1 EndZ=0
    g249: LineSegment StartX=288.775 StartY=-45.1 StartZ=0 EndX=301.775 EndY=-45.1 EndZ=0
    g250: LineSegment StartX=288.275 StartY=-31.6 StartZ=0 EndX=288.275 EndY=-44.6 EndZ=0
    g251: LineSegment StartX=302.275 StartY=-31.6 StartZ=0 EndX=302.275 EndY=-44.6 EndZ=0
    g252: ArcOfCircle CenterX=288.775 CenterY=-31.6 CenterZ=0 NormalX=0 NormalY=0 NormalZ=1 AngleXU=0 Radius=0.5 StartAngle=1.5708 EndAngle=3.14159
    g253: ArcOfCircle CenterX=301.775 CenterY=-31.6 CenterZ=0 NormalX=0 NormalY=0 NormalZ=1 AngleXU=0 Radius=0.5 StartAngle=0 EndAngle=1.5708
    g254: ArcOfCircle CenterX=288.775 CenterY=-44.6 CenterZ=0 NormalX=0 NormalY=0 NormalZ=1 AngleXU=0 Radius=0.5 StartAngle=3.14159 EndAngle=4.71239
    g255: ArcOfCircle CenterX=301.775 CenterY=-44.6 CenterZ=0 NormalX=0 NormalY=0 NormalZ=1 AngleXU=0 Radius=0.5 StartAngle=4.71239 EndAngle=6.28319
    g256: LineSegment StartX=336.4 StartY=-31.1 StartZ=0 EndX=349.4 EndY=-31.1 EndZ=0
    g257: LineSegment StartX=336.4 StartY=-45.1 StartZ=0 EndX=349.4 EndY=-45.1 EndZ=0
    g258: LineSegment StartX=335.9 StartY=-31.6 StartZ=0 EndX=335.9 EndY=-44.6 EndZ=0
    g259: LineSegment StartX=349.9 StartY=-31.6 StartZ=0 EndX=349.9 EndY=-44.6 EndZ=0
    g260: ArcOfCircle CenterX=336.4 CenterY=-31.6 CenterZ=0 NormalX=0 NormalY=0 NormalZ=1 AngleXU=0 Radius=0.5 StartAngle=1.5708 EndAngle=3.14159
    g261: ArcOfCircle CenterX=349.4 CenterY=-31.6 CenterZ=0 NormalX=0 NormalY=0 NormalZ=1 AngleXU=0 Radius=0.5 StartAngle=0 EndAngle=1.5708
    g262: ArcOfCircle CenterX=336.4 CenterY=-44.6 CenterZ=0 NormalX=0 NormalY=0 NormalZ=1 AngleXU=0 Radius=0.5 StartAngle=3.14159 EndAngle=4.71239
    g263: ArcOfCircle CenterX=349.4 CenterY=-44.6 CenterZ=0 NormalX=0 NormalY=0 NormalZ=1 AngleXU=0 Radius=0.5 StartAngle=4.71239 EndAngle=6.28319
    g264: LineSegment StartX=3.025 StartY=-50.15 StartZ=0 EndX=16.025 EndY=-50.15 EndZ=0
    g265: LineSegment StartX=3.025 StartY=-64.15 StartZ=0 EndX=16.025 EndY=-64.15 EndZ=0
    g266: LineSegment StartX=2.525 StartY=-50.65 StartZ=0 EndX=2.525 EndY=-63.65 EndZ=0
    g267: LineSegment StartX=16.525 StartY=-50.65 StartZ=0 EndX=16.525 EndY=-63.65 EndZ=0
    g268: ArcOfCircle CenterX=3.025 CenterY=-50.65 CenterZ=0 NormalX=0 NormalY=0 NormalZ=1 AngleXU=0 Radius=0.5 StartAngle=1.5708 EndAngle=3.14159
    g269: ArcOfCircle CenterX=16.025 CenterY=-50.65 CenterZ=0 NormalX=0 NormalY=0 NormalZ=1 AngleXU=0 Radius=0.5 StartAngle=0 EndAngle=1.5708
    g270: ArcOfCircle CenterX=3.025 CenterY=-63.65 CenterZ=0 NormalX=0 NormalY=0 NormalZ=1 AngleXU=0 Radius=0.5 StartAngle=3.14159 EndAngle=4.71239
    g271: ArcOfCircle CenterX=16.025 CenterY=-63.65 CenterZ=0 NormalX=0 NormalY=0 NormalZ=1 AngleXU=0 Radius=0.5 StartAngle=4.71239 EndAngle=6.28319
    g272: LineSegment StartX=22.075 StartY=-50.15 StartZ=0 EndX=35.075 EndY=-50.15 EndZ=0
    g273: LineSegment StartX=22.075 StartY=-64.15 StartZ=0 EndX=35.075 EndY=-64.15 EndZ=0
    g274: LineSegment StartX=21.575 StartY=-50.65 StartZ=0 EndX=21.575 EndY=-63.65 EndZ=0
    g275: LineSegment StartX=35.575 StartY=-50.65 StartZ=0 EndX=35.575 EndY=-63.65 EndZ=0
    g276: ArcOfCircle CenterX=22.075 CenterY=-50.65 CenterZ=0 NormalX=0 NormalY=0 NormalZ=1 AngleXU=0 Radius=0.5 StartAngle=1.5708 EndAngle=3.14159
    g277: ArcOfCircle CenterX=35.075 CenterY=-50.65 CenterZ=0 NormalX=0 NormalY=0 NormalZ=1 AngleXU=0 Radius=0.5 StartAngle=0 EndAngle=1.5708
    g278: ArcOfCircle CenterX=22.075 CenterY=-63.65 CenterZ=0 NormalX=0 NormalY=0 NormalZ=1 AngleXU=0 Radius=0.5 StartAngle=3.14159 EndAngle=4.71239
    g279: ArcOfCircle CenterX=35.075 CenterY=-63.65 CenterZ=0 NormalX=0 NormalY=0 NormalZ=1 AngleXU=0 Radius=0.5 StartAngle=4.71239 EndAngle=6.28319
    g280: LineSegment StartX=41.125 StartY=-50.15 StartZ=0 EndX=54.125 EndY=-50.15 EndZ=0
    g281: LineSegment StartX=41.125 StartY=-64.15 StartZ=0 EndX=54.125 EndY=-64.15 EndZ=0
    g282: LineSegment StartX=40.625 StartY=-50.65 StartZ=0 EndX=40.625 EndY=-63.65 EndZ=0
    g283: LineSegment StartX=54.625 StartY=-50.65 StartZ=0 EndX=54.625 EndY=-63.65 EndZ=0
    g284: ArcOfCircle CenterX=41.125 CenterY=-50.65 CenterZ=0 NormalX=0 NormalY=0 NormalZ=1 AngleXU=0 Radius=0.5 StartAngle=1.5708 EndAngle=3.14159
    g285: ArcOfCircle CenterX=54.125 CenterY=-50.65 CenterZ=0 NormalX=0 NormalY=0 NormalZ=1 AngleXU=0 Radius=0.5 StartAngle=0 EndAngle=1.5708
    g286: ArcOfCircle CenterX=41.125 CenterY=-63.65 CenterZ=0 NormalX=0 NormalY=0 NormalZ=1 AngleXU=0 Radius=0.5 StartAngle=3.14159 EndAngle=4.71239
    g287: ArcOfCircle CenterX=54.125 CenterY=-63.65 CenterZ=0 NormalX=0 NormalY=0 NormalZ=1 AngleXU=0 Radius=0.5 StartAngle=4.71239 EndAngle=6.28319
    g288: LineSegment StartX=60.175 StartY=-50.15 StartZ=0 EndX=73.175 EndY=-50.15 EndZ=0
    g289: LineSegment StartX=60.175 StartY=-64.15 StartZ=0 EndX=73.175 EndY=-64.15 EndZ=0
    g290: LineSegment StartX=59.675 StartY=-50.65 StartZ=0 EndX=59.675 EndY=-63.65 EndZ=0
    g291: LineSegment StartX=73.675 StartY=-50.65 StartZ=0 EndX=73.675 EndY=-63.65 EndZ=0
    g292: ArcOfCircle CenterX=60.175 CenterY=-50.65 CenterZ=0 NormalX=0 NormalY=0 NormalZ=1 AngleXU=0 Radius=0.5 StartAngle=1.5708 EndAngle=3.14159
    g293: ArcOfCircle CenterX=73.175 CenterY=-50.65 CenterZ=0 NormalX=0 NormalY=0 NormalZ=1 AngleXU=0 Radius=0.5 StartAngle=0 EndAngle=1.5708
    g294: ArcOfCircle CenterX=60.175 CenterY=-63.65 CenterZ=0 NormalX=0 NormalY=0 NormalZ=1 AngleXU=0 Radius=0.5 StartAngle=3.14159 EndAngle=4.71239
    g295: ArcOfCircle CenterX=73.175 CenterY=-63.65 CenterZ=0 NormalX=0 NormalY=0 NormalZ=1 AngleXU=0 Radius=0.5 StartAngle=4.71239 EndAngle=6.28319
    g296: LineSegment StartX=79.225 StartY=-50.15 StartZ=0 EndX=92.225 EndY=-50.15 EndZ=0
    g297: LineSegment StartX=79.225 StartY=-64.15 StartZ=0 EndX=92.225 EndY=-64.15 EndZ=0
    g298: LineSegment StartX=78.725 StartY=-50.65 StartZ=0 EndX=78.725 EndY=-63.65 EndZ=0
    g299: LineSegment StartX=92.725 StartY=-50.65 StartZ=0 EndX=92.725 EndY=-63.65 EndZ=0
    g300: ArcOfCircle CenterX=79.225 CenterY=-50.65 CenterZ=0 NormalX=0 NormalY=0 NormalZ=1 AngleXU=0 Radius=0.5 StartAngle=1.5708 EndAngle=3.14159
    g301: ArcOfCircle CenterX=92.225 CenterY=-50.65 CenterZ=0 NormalX=0 NormalY=0 NormalZ=1 AngleXU=0 Radius=0.5 StartAngle=0 EndAngle=1.5708
    g302: ArcOfCircle CenterX=79.225 CenterY=-63.65 CenterZ=0 NormalX=0 NormalY=0 NormalZ=1 AngleXU=0 Radius=0.5 StartAngle=3.14159 EndAngle=4.71239
    g303: ArcOfCircle CenterX=92.225 CenterY=-63.65 CenterZ=0 NormalX=0 NormalY=0 NormalZ=1 AngleXU=0 Radius=0.5 StartAngle=4.71239 EndAngle=6.28319
    g304: LineSegment StartX=98.275 StartY=-50.15 StartZ=0 EndX=111.275 EndY=-50.15 EndZ=0
    g305: LineSegment StartX=98.275 StartY=-64.15 StartZ=0 EndX=111.275 EndY=-64.15 EndZ=0
    g306: LineSegment StartX=97.775 StartY=-50.65 StartZ=0 EndX=97.775 EndY=-63.65 EndZ=0
    g307: LineSegment StartX=111.775 StartY=-50.65 StartZ=0 EndX=111.775 EndY=-63.65 EndZ=0
    g308: ArcOfCircle CenterX=98.275 CenterY=-50.65 CenterZ=0 NormalX=0 NormalY=0 NormalZ=1 AngleXU=0 Radius=0.5 StartAngle=1.5708 EndAngle=3.14159
    g309: ArcOfCircle CenterX=111.275 CenterY=-50.65 CenterZ=0 NormalX=0 NormalY=0 NormalZ=1 AngleXU=0 Radius=0.5 StartAngle=0 EndAngle=1.5708
    g310: ArcOfCircle CenterX=98.275 CenterY=-63.65 CenterZ=0 NormalX=0 NormalY=0 NormalZ=1 AngleXU=0 Radius=0.5 StartAngle=3.14159 EndAngle=4.71239
    g311: ArcOfCircle CenterX=111.275 CenterY=-63.65 CenterZ=0 NormalX=0 NormalY=0 NormalZ=1 AngleXU=0 Radius=0.5 StartAngle=4.71239 EndAngle=6.28319
    g312: LineSegment StartX=117.325 StartY=-50.15 StartZ=0 EndX=130.325 EndY=-50.15 EndZ=0
    g313: LineSegment StartX=117.325 StartY=-64.15 StartZ=0 EndX=130.325 EndY=-64.15 EndZ=0
    g314: LineSegment StartX=116.825 StartY=-50.65 StartZ=0 EndX=116.825 EndY=-63.65 EndZ=0
    g315: LineSegment StartX=130.825 StartY=-50.65 StartZ=0 EndX=130.825 EndY=-63.65 EndZ=0
    g316: ArcOfCircle CenterX=117.325 CenterY=-50.65 CenterZ=0 NormalX=0 NormalY=0 NormalZ=1 AngleXU=0 Radius=0.5 StartAngle=1.5708 EndAngle=3.14159
    g317: ArcOfCircle CenterX=130.325 CenterY=-50.65 CenterZ=0 NormalX=0 NormalY=0 NormalZ=1 AngleXU=0 Radius=0.5 StartAngle=0 EndAngle=1.5708
    g318: ArcOfCircle CenterX=117.325 CenterY=-63.65 CenterZ=0 NormalX=0 NormalY=0 NormalZ=1 AngleXU=0 Radius=0.5 StartAngle=3.14159 EndAngle=4.71239
    g319: ArcOfCircle CenterX=130.325 CenterY=-63.65 CenterZ=0 NormalX=0 NormalY=0 NormalZ=1 AngleXU=0 Radius=0.5 StartAngle=4.71239 EndAngle=6.28319
    g320: LineSegment StartX=136.375 StartY=-50.15 StartZ=0 EndX=149.375 EndY=-50.15 EndZ=0
    g321: LineSegment StartX=136.375 StartY=-64.15 StartZ=0 EndX=149.375 EndY=-64.15 EndZ=0
    g322: LineSegment StartX=135.875 StartY=-50.65 StartZ=0 EndX=135.875 EndY=-63.65 EndZ=0
    g323: LineSegment StartX=149.875 StartY=-50.65 StartZ=0 EndX=149.875 EndY=-63.65 EndZ=0
    g324: ArcOfCircle CenterX=136.375 CenterY=-50.65 CenterZ=0 NormalX=0 NormalY=0 NormalZ=1 AngleXU=0 Radius=0.5 StartAngle=1.5708 EndAngle=3.14159
    g325: ArcOfCircle CenterX=149.375 CenterY=-50.65 CenterZ=0 NormalX=0 NormalY=0 NormalZ=1 AngleXU=0 Radius=0.5 StartAngle=0 EndAngle=1.5708
    g326: ArcOfCircle CenterX=136.375 CenterY=-63.65 CenterZ=0 NormalX=0 NormalY=0 NormalZ=1 AngleXU=0 Radius=0.5 StartAngle=3.14159 EndAngle=4.71239
    g327: ArcOfCircle CenterX=149.375 CenterY=-63.65 CenterZ=0 NormalX=0 NormalY=0 NormalZ=1 AngleXU=0 Radius=0.5 StartAngle=4.71239 EndAngle=6.28319
    g328: LineSegment StartX=155.425 StartY=-50.15 StartZ=0 EndX=168.425 EndY=-50.15 EndZ=0
    g329: LineSegment StartX=155.425 StartY=-64.15 StartZ=0 EndX=168.425 EndY=-64.15 EndZ=0
    g330: LineSegment StartX=154.925 StartY=-50.65 StartZ=0 EndX=154.925 EndY=-63.65 EndZ=0
    g331: LineSegment StartX=168.925 StartY=-50.65 StartZ=0 EndX=168.925 EndY=-63.65 EndZ=0
    g332: ArcOfCircle CenterX=155.425 CenterY=-50.65 CenterZ=0 NormalX=0 NormalY=0 NormalZ=1 AngleXU=0 Radius=0.5 StartAngle=1.5708 EndAngle=3.14159
    g333: ArcOfCircle CenterX=168.425 CenterY=-50.65 CenterZ=0 NormalX=0 NormalY=0 NormalZ=1 AngleXU=0 Radius=0.5 StartAngle=0 EndAngle=1.5708
    g334: ArcOfCircle CenterX=155.425 CenterY=-63.65 CenterZ=0 NormalX=0 NormalY=0 NormalZ=1 AngleXU=0 Radius=0.5 StartAngle=3.14159 EndAngle=4.71239
    g335: ArcOfCircle CenterX=168.425 CenterY=-63.65 CenterZ=0 NormalX=0 NormalY=0 NormalZ=1 AngleXU=0 Radius=0.5 StartAngle=4.71239 EndAngle=6.28319
    g336: LineSegment StartX=174.475 StartY=-50.15 StartZ=0 EndX=187.475 EndY=-50.15 EndZ=0
    g337: LineSegment StartX=174.475 StartY=-64.15 StartZ=0 EndX=187.475 EndY=-64.15 EndZ=0
    g338: LineSegment StartX=173.975 StartY=-50.65 StartZ=0 EndX=173.975 EndY=-63.65 EndZ=0
    g339: LineSegment StartX=187.975 StartY=-50.65 StartZ=0 EndX=187.975 EndY=-63.65 EndZ=0
    g340: ArcOfCircle CenterX=174.475 CenterY=-50.65 CenterZ=0 NormalX=0 NormalY=0 NormalZ=1 AngleXU=0 Radius=0.5 StartAngle=1.5708 EndAngle=3.14159
    g341: ArcOfCircle CenterX=187.475 CenterY=-50.65 CenterZ=0 NormalX=0 NormalY=0 NormalZ=1 AngleXU=0 Radius=0.5 StartAngle=0 EndAngle=1.5708
    g342: ArcOfCircle CenterX=174.475 CenterY=-63.65 CenterZ=0 NormalX=0 NormalY=0 NormalZ=1 AngleXU=0 Radius=0.5 StartAngle=3.14159 EndAngle=4.71239
    g343: ArcOfCircle CenterX=187.475 CenterY=-63.65 CenterZ=0 NormalX=0 NormalY=0 NormalZ=1 AngleXU=0 Radius=0.5 StartAngle=4.71239 EndAngle=6.28319
    g344: LineSegment StartX=193.525 StartY=-50.15 StartZ=0 EndX=206.525 EndY=-50.15 EndZ=0
    g345: LineSegment StartX=193.525 StartY=-64.15 StartZ=0 EndX=206.525 EndY=-64.15 EndZ=0
    g346: LineSegment StartX=193.025 StartY=-50.65 StartZ=0 EndX=193.025 EndY=-63.65 EndZ=0
    g347: LineSegment StartX=207.025 StartY=-50.65 StartZ=0 EndX=207.025 EndY=-63.65 EndZ=0
    g348: ArcOfCircle CenterX=193.525 CenterY=-50.65 CenterZ=0 NormalX=0 NormalY=0 NormalZ=1 AngleXU=0 Radius=0.5 StartAngle=1.5708 EndAngle=3.14159
    g349: ArcOfCircle CenterX=206.525 CenterY=-50.65 CenterZ=0 NormalX=0 NormalY=0 NormalZ=1 AngleXU=0 Radius=0.5 StartAngle=0 EndAngle=1.5708
    g350: ArcOfCircle CenterX=193.525 CenterY=-63.65 CenterZ=0 NormalX=0 NormalY=0 NormalZ=1 AngleXU=0 Radius=0.5 StartAngle=3.14159 EndAngle=4.71239
    g351: ArcOfCircle CenterX=206.525 CenterY=-63.65 CenterZ=0 NormalX=0 NormalY=0 NormalZ=1 AngleXU=0 Radius=0.5 StartAngle=4.71239 EndAngle=6.28319
    g352: LineSegment StartX=212.575 StartY=-50.15 StartZ=0 EndX=225.575 EndY=-50.15 EndZ=0
    g353: LineSegment StartX=212.575 StartY=-64.15 StartZ=0 EndX=225.575 EndY=-64.15 EndZ=0
    g354: LineSegment StartX=212.075 StartY=-50.65 StartZ=0 EndX=212.075 EndY=-63.65 EndZ=0
    g355: LineSegment StartX=226.075 StartY=-50.65 StartZ=0 EndX=226.075 EndY=-63.65 EndZ=0
    g356: ArcOfCircle CenterX=212.575 CenterY=-50.65 CenterZ=0 NormalX=0 NormalY=0 NormalZ=1 AngleXU=0 Radius=0.5 StartAngle=1.5708 EndAngle=3.14159
    g357: ArcOfCircle CenterX=225.575 CenterY=-50.65 CenterZ=0 NormalX=0 NormalY=0 NormalZ=1 AngleXU=0 Radius=0.5 StartAngle=0 EndAngle=1.5708
    g358: ArcOfCircle CenterX=212.575 CenterY=-63.65 CenterZ=0 NormalX=0 NormalY=0 NormalZ=1 AngleXU=0 Radius=0.5 StartAngle=3.14159 EndAngle=4.71239
    g359: ArcOfCircle CenterX=225.575 CenterY=-63.65 CenterZ=0 NormalX=0 NormalY=0 NormalZ=1 AngleXU=0 Radius=0.5 StartAngle=4.71239 EndAngle=6.28319
    g360: LineSegment StartX=231.625 StartY=-50.15 StartZ=0 EndX=244.625 EndY=-50.15 EndZ=0
    g361: LineSegment StartX=231.625 StartY=-64.15 StartZ=0 EndX=244.625 EndY=-64.15 EndZ=0
    g362: LineSegment StartX=231.125 StartY=-50.65 StartZ=0 EndX=231.125 EndY=-63.65 EndZ=0
    g363: LineSegment StartX=245.125 StartY=-50.65 StartZ=0 EndX=245.125 EndY=-63.65 EndZ=0
    g364: ArcOfCircle CenterX=231.625 CenterY=-50.65 CenterZ=0 NormalX=0 NormalY=0 NormalZ=1 AngleXU=0 Radius=0.5 StartAngle=1.5708 EndAngle=3.14159
    g365: ArcOfCircle CenterX=244.625 CenterY=-50.65 CenterZ=0 NormalX=0 NormalY=0 NormalZ=1 AngleXU=0 Radius=0.5 StartAngle=0 EndAngle=1.5708
    g366: ArcOfCircle CenterX=231.625 CenterY=-63.65 CenterZ=0 NormalX=0 NormalY=0 NormalZ=1 AngleXU=0 Radius=0.5 StartAngle=3.14159 EndAngle=4.71239
    g367: ArcOfCircle CenterX=244.625 CenterY=-63.65 CenterZ=0 NormalX=0 NormalY=0 NormalZ=1 AngleXU=0 Radius=0.5 StartAngle=4.71239 EndAngle=6.28319
    g368: LineSegment StartX=264.175 StartY=-60.175 StartZ=0 EndX=264.175 EndY=-73.175 EndZ=0
    g369: LineSegment StartX=250.175 StartY=-60.175 StartZ=0 EndX=250.175 EndY=-73.175 EndZ=0
    g370: LineSegment StartX=263.675 StartY=-59.675 StartZ=0 EndX=250.675 EndY=-59.675 EndZ=0
    g371: LineSegment StartX=263.675 StartY=-73.675 StartZ=0 EndX=250.675 EndY=-73.675 EndZ=0
    g372: ArcOfCircle CenterX=263.675 CenterY=-60.175 CenterZ=0 NormalX=0 NormalY=0 NormalZ=1 AngleXU=0 Radius=0.5 StartAngle=0 EndAngle=1.5708
    g373: ArcOfCircle CenterX=263.675 CenterY=-73.175 CenterZ=0 NormalX=0 NormalY=0 NormalZ=1 AngleXU=0 Radius=0.5 StartAngle=4.71239 EndAngle=6.28319
    g374: ArcOfCircle CenterX=250.675 CenterY=-60.175 CenterZ=0 NormalX=0 NormalY=0 NormalZ=1 AngleXU=0 Radius=0.5 StartAngle=1.5708 EndAngle=3.14159
    g375: ArcOfCircle CenterX=250.675 CenterY=-73.175 CenterZ=0 NormalX=0 NormalY=0 NormalZ=1 AngleXU=0 Radius=0.5 StartAngle=3.14159 EndAngle=4.71239
    g376: LineSegment StartX=263.175 StartY=-51.737 StartZ=0 EndX=263.175 EndY=-57.737 EndZ=0
    g377: LineSegment StartX=248.175 StartY=-51.737 StartZ=0 EndX=248.175 EndY=-57.737 EndZ=0
    g378: LineSegment StartX=262.675 StartY=-51.237 StartZ=0 EndX=248.675 EndY=-51.237 EndZ=0
    g379: LineSegment StartX=262.675 StartY=-58.237 StartZ=0 EndX=248.675 EndY=-58.237 EndZ=0
    g380: ArcOfCircle CenterX=262.675 CenterY=-51.737 CenterZ=0 NormalX=0 NormalY=0 NormalZ=1 AngleXU=0 Radius=0.5 StartAngle=0 EndAngle=1.5708
    g381: ArcOfCircle CenterX=262.675 CenterY=-57.737 CenterZ=0 NormalX=0 NormalY=0 NormalZ=1 AngleXU=0 Radius=0.5 StartAngle=4.71239 EndAngle=6.28319
    g382: ArcOfCircle CenterX=248.675 CenterY=-51.737 CenterZ=0 NormalX=0 NormalY=0 NormalZ=1 AngleXU=0 Radius=0.5 StartAngle=1.5708 EndAngle=3.14159
    g383: ArcOfCircle CenterX=248.675 CenterY=-57.737 CenterZ=0 NormalX=0 NormalY=0 NormalZ=1 AngleXU=0 Radius=0.5 StartAngle=3.14159 EndAngle=4.71239
    g384: LineSegment StartX=263.175 StartY=-75.613 StartZ=0 EndX=263.175 EndY=-81.613 EndZ=0
    g385: LineSegment StartX=248.175 StartY=-75.613 StartZ=0 EndX=248.175 EndY=-81.613 EndZ=0
    g386: LineSegment StartX=262.675 StartY=-75.113 StartZ=0 EndX=248.675 EndY=-75.113 EndZ=0
    g387: LineSegment StartX=262.675 StartY=-82.113 StartZ=0 EndX=248.675 EndY=-82.113 EndZ=0
    g388: ArcOfCircle CenterX=262.675 CenterY=-75.613 CenterZ=0 NormalX=0 NormalY=0 NormalZ=1 AngleXU=0 Radius=0.5 StartAngle=0 EndAngle=1.5708
    g389: ArcOfCircle CenterX=262.675 CenterY=-81.613 CenterZ=0 NormalX=0 NormalY=0 NormalZ=1 AngleXU=0 Radius=0.5 StartAngle=4.71239 EndAngle=6.28319
    g390: ArcOfCircle CenterX=248.675 CenterY=-75.613 CenterZ=0 NormalX=0 NormalY=0 NormalZ=1 AngleXU=0 Radius=0.5 StartAngle=1.5708 EndAngle=3.14159
    g391: ArcOfCircle CenterX=248.675 CenterY=-81.613 CenterZ=0 NormalX=0 NormalY=0 NormalZ=1 AngleXU=0 Radius=0.5 StartAngle=3.14159 EndAngle=4.71239
    g392: LineSegment StartX=269.725 StartY=-50.15 StartZ=0 EndX=282.725 EndY=-50.15 EndZ=0
    g393: LineSegment StartX=269.725 StartY=-64.15 StartZ=0 EndX=282.725 EndY=-64.15 EndZ=0
    g394: LineSegment StartX=269.225 StartY=-50.65 StartZ=0 EndX=269.225 EndY=-63.65 EndZ=0
    g395: LineSegment StartX=283.225 StartY=-50.65 StartZ=0 EndX=283.225 EndY=-63.65 EndZ=0
    g396: ArcOfCircle CenterX=269.725 CenterY=-50.65 CenterZ=0 NormalX=0 NormalY=0 NormalZ=1 AngleXU=0 Radius=0.5 StartAngle=1.5708 EndAngle=3.14159
    g397: ArcOfCircle CenterX=282.725 CenterY=-50.65 CenterZ=0 NormalX=0 NormalY=0 NormalZ=1 AngleXU=0 Radius=0.5 StartAngle=0 EndAngle=1.5708
    g398: ArcOfCircle CenterX=269.725 CenterY=-63.65 CenterZ=0 NormalX=0 NormalY=0 NormalZ=1 AngleXU=0 Radius=0.5 StartAngle=3.14159 EndAngle=4.71239
    g399: ArcOfCircle CenterX=282.725 CenterY=-63.65 CenterZ=0 NormalX=0 NormalY=0 NormalZ=1 AngleXU=0 Radius=0.5 StartAngle=4.71239 EndAngle=6.28319
    ... +416 more geometry lines
  constraints (816):
    c: Coincident(g682,g686)
    c: Coincident(g682,g684)
    c: Coincident(g546,g550)
    c: Coincident(g546,g548)
    c: Coincident(g418,g422)
    c: Coincident(g418,g420)
    c: Coincident(g266,g270)
    c: Coincident(g266,g268)
    c: Coincident(g130,g134)
    c: Coincident(g130,g132)
    c: Coincident(g2,g6)
    c: Coincident(g2,g4)
    c: Coincident(g681,g686)
    c: Coincident(g680,g684)
    c: Coincident(g545,g550)
    c: Coincident(g544,g548)
    c: Coincident(g417,g422)
    c: Coincident(g416,g420)
    c: Coincident(g265,g270)
    c: Coincident(g264,g268)
    c: Coincident(g129,g134)
    c: Coincident(g128,g132)
    c: Coincident(g1,g6)
    c: Coincident(g0,g4)
    c: Coincident(g681,g687)
    c: Coincident(g680,g685)
    c: Coincident(g545,g551)
    c: Coincident(g544,g549)
    c: Coincident(g417,g423)
    c: Coincident(g416,g421)
    c: Coincident(g265,g271)
    c: Coincident(g264,g269)
    c: Coincident(g129,g135)
    c: Coincident(g128,g133)
    c: Coincident(g1,g7)
    c: Coincident(g0,g5)
    c: Coincident(g683,g687)
    c: Coincident(g683,g685)
    c: Coincident(g547,g551)
    c: Coincident(g547,g549)
    c: Coincident(g419,g423)
    c: Coincident(g419,g421)
    c: Coincident(g267,g271)
    c: Coincident(g267,g269)
    c: Coincident(g131,g135)
    c: Coincident(g131,g133)
    c: Coincident(g3,g7)
    c: Coincident(g3,g5)
    c: Coincident(g690,g694)
    c: Coincident(g690,g692)
    c: Coincident(g554,g558)
    c: Coincident(g554,g556)
    c: Coincident(g426,g430)
    c: Coincident(g426,g428)
    c: Coincident(g274,g278)
    c: Coincident(g274,g276)
    c: Coincident(g138,g142)
    c: Coincident(g138,g140)
    c: Coincident(g10,g14)
    c: Coincident(g10,g12)
    c: Coincident(g689,g694)
    c: Coincident(g688,g692)
    c: Coincident(g553,g558)
    c: Coincident(g552,g556)
    c: Coincident(g425,g430)
    c: Coincident(g424,g428)
    c: Coincident(g273,g278)
    c: Coincident(g272,g276)
    c: Coincident(g137,g142)
    c: Coincident(g136,g140)
    c: Coincident(g9,g14)
    c: Coincident(g8,g12)
    c: Coincident(g689,g695)
    c: Coincident(g688,g693)
    c: Coincident(g553,g559)
    c: Coincident(g552,g557)
    c: Coincident(g425,g431)
    c: Coincident(g424,g429)
    c: Coincident(g273,g279)
    c: Coincident(g272,g277)
    c: Coincident(g137,g143)
    c: Coincident(g136,g141)
    c: Coincident(g9,g15)
    c: Coincident(g8,g13)
    c: Coincident(g691,g695)
    c: Coincident(g691,g693)
    c: Coincident(g555,g559)
    c: Coincident(g555,g557)
    c: Coincident(g427,g431)
    c: Coincident(g427,g429)
    c: Coincident(g275,g279)
    c: Coincident(g275,g277)
    c: Coincident(g139,g143)
    c: Coincident(g139,g141)
    c: Coincident(g11,g15)
    c: Coincident(g11,g13)
    c: Coincident(g698,g702)
    c: Coincident(g698,g700)
    c: Coincident(g562,g566)
    c: Coincident(g562,g564)
    c: Coincident(g434,g438)
    c: Coincident(g434,g436)
    c: Coincident(g282,g286)
    c: Coincident(g282,g284)
    c: Coincident(g146,g150)
    c: Coincident(g146,g148)
    c: Coincident(g18,g22)
    c: Coincident(g18,g20)
    c: Coincident(g697,g702)
    c: Coincident(g696,g700)
    c: Coincident(g561,g566)
    c: Coincident(g560,g564)
    c: Coincident(g433,g438)
    c: Coincident(g432,g436)
    c: Coincident(g281,g286)
    c: Coincident(g280,g284)
    c: Coincident(g145,g150)
    c: Coincident(g144,g148)
    c: Coincident(g17,g22)
    c: Coincident(g16,g20)
    c: Coincident(g697,g703)
    c: Coincident(g696,g701)
    c: Coincident(g561,g567)
    c: Coincident(g560,g565)
    c: Coincident(g433,g439)
    c: Coincident(g432,g437)
    c: Coincident(g281,g287)
    c: Coincident(g280,g285)
    c: Coincident(g145,g151)
    c: Coincident(g144,g149)
    c: Coincident(g17,g23)
    c: Coincident(g16,g21)
    c: Coincident(g699,g703)
    c: Coincident(g699,g701)
    c: Coincident(g563,g567)
    c: Coincident(g563,g565)
    c: Coincident(g435,g439)
    c: Coincident(g435,g437)
    c: Coincident(g283,g287)
    c: Coincident(g283,g285)
    c: Coincident(g147,g151)
    c: Coincident(g147,g149)
    c: Coincident(g19,g23)
    c: Coincident(g19,g21)
    c: Coincident(g570,g574)
    c: Coincident(g570,g572)
    c: Coincident(g442,g446)
    c: Coincident(g442,g444)
    c: Coincident(g290,g294)
    c: Coincident(g290,g292)
    c: Coincident(g154,g158)
    c: Coincident(g154,g156)
    c: Coincident(g26,g30)
    c: Coincident(g26,g28)
    c: Coincident(g569,g574)
    c: Coincident(g568,g572)
    c: Coincident(g441,g446)
    c: Coincident(g440,g444)
    c: Coincident(g289,g294)
    c: Coincident(g288,g292)
    c: Coincident(g153,g158)
    c: Coincident(g152,g156)
    c: Coincident(g25,g30)
    c: Coincident(g24,g28)
    c: Coincident(g706,g710)
    c: Coincident(g706,g708)
    c: Coincident(g705,g710)
    c: Coincident(g704,g708)
    c: Coincident(g569,g575)
    c: Coincident(g568,g573)
    c: Coincident(g441,g447)
    c: Coincident(g440,g445)
    c: Coincident(g289,g295)
    c: Coincident(g288,g293)
    c: Coincident(g153,g159)
    c: Coincident(g152,g157)
    c: Coincident(g25,g31)
    c: Coincident(g24,g29)
    c: Coincident(g571,g575)
    c: Coincident(g571,g573)
    c: Coincident(g443,g447)
    c: Coincident(g443,g445)
    c: Coincident(g291,g295)
    c: Coincident(g291,g293)
    c: Coincident(g155,g159)
    c: Coincident(g155,g157)
    c: Coincident(g27,g31)
    c: Coincident(g27,g29)
    c: Coincident(g705,g711)
    c: Coincident(g704,g709)
    c: Coincident(g707,g711)
    c: Coincident(g707,g709)
    c: Coincident(g578,g582)
    c: Coincident(g578,g580)
    c: Coincident(g450,g454)
    c: Coincident(g450,g452)
    c: Coincident(g298,g302)
    c: Coincident(g298,g300)
    c: Coincident(g162,g166)
    c: Coincident(g162,g164)
    c: Coincident(g34,g38)
    c: Coincident(g34,g36)
    c: Coincident(g577,g582)
    c: Coincident(g576,g580)
    c: Coincident(g449,g454)
    c: Coincident(g448,g452)
    c: Coincident(g297,g302)
    c: Coincident(g296,g300)
    c: Coincident(g161,g166)
    c: Coincident(g160,g164)
    c: Coincident(g33,g38)
    c: Coincident(g32,g36)
    c: Coincident(g722,g726)
    c: Coincident(g722,g724)
    c: Coincident(g721,g726)
    c: Coincident(g720,g724)
    c: Coincident(g577,g583)
    c: Coincident(g576,g581)
    c: Coincident(g449,g455)
    c: Coincident(g448,g453)
    c: Coincident(g297,g303)
    c: Coincident(g296,g301)
    c: Coincident(g161,g167)
    c: Coincident(g160,g165)
    c: Coincident(g33,g39)
    c: Coincident(g32,g37)
    c: Coincident(g579,g583)
    c: Coincident(g579,g581)
    c: Coincident(g451,g455)
    c: Coincident(g451,g453)
    c: Coincident(g299,g303)
    c: Coincident(g299,g301)
    c: Coincident(g163,g167)
    c: Coincident(g163,g165)
    c: Coincident(g35,g39)
    c: Coincident(g35,g37)
    c: Coincident(g586,g590)
    c: Coincident(g586,g588)
    c: Coincident(g458,g462)
    c: Coincident(g458,g460)
    c: Coincident(g306,g310)
    c: Coincident(g306,g308)
    c: Coincident(g170,g174)
    c: Coincident(g170,g172)
    c: Coincident(g42,g46)
    c: Coincident(g42,g44)
    c: Coincident(g721,g727)
    c: Coincident(g720,g725)
    c: Coincident(g585,g590)
    c: Coincident(g584,g588)
    c: Coincident(g457,g462)
    c: Coincident(g456,g460)
    c: Coincident(g305,g310)
    c: Coincident(g304,g308)
    c: Coincident(g169,g174)
    c: Coincident(g168,g172)
    c: Coincident(g41,g46)
    c: Coincident(g40,g44)
    c: Coincident(g723,g727)
    c: Coincident(g723,g725)
    c: Coincident(g714,g718)
    c: Coincident(g714,g716)
    c: Coincident(g713,g718)
    c: Coincident(g712,g716)
    c: Coincident(g585,g591)
    c: Coincident(g584,g589)
    c: Coincident(g457,g463)
    c: Coincident(g456,g461)
    c: Coincident(g305,g311)
    c: Coincident(g304,g309)
    c: Coincident(g169,g175)
    c: Coincident(g168,g173)
    c: Coincident(g41,g47)
    c: Coincident(g40,g45)
    c: Coincident(g587,g591)
    c: Coincident(g587,g589)
    c: Coincident(g459,g463)
    c: Coincident(g459,g461)
    c: Coincident(g307,g311)
    c: Coincident(g307,g309)
    c: Coincident(g171,g175)
    c: Coincident(g171,g173)
    c: Coincident(g43,g47)
    c: Coincident(g43,g45)
    c: Coincident(g713,g719)
    c: Coincident(g712,g717)
    c: Coincident(g715,g719)
    c: Coincident(g715,g717)
    c: Coincident(g730,g734)
    c: Coincident(g730,g732)
    c: Coincident(g729,g734)
    c: Coincident(g728,g732)
    c: Coincident(g594,g598)
    c: Coincident(g594,g596)
    c: Coincident(g466,g470)
    c: Coincident(g466,g468)
    c: Coincident(g314,g318)
    c: Coincident(g314,g316)
    c: Coincident(g178,g182)
    c: Coincident(g178,g180)
    c: Coincident(g50,g54)
    c: Coincident(g50,g52)
    c: Coincident(g593,g598)
    c: Coincident(g592,g596)
    c: Coincident(g465,g470)
    c: Coincident(g464,g468)
    c: Coincident(g313,g318)
    c: Coincident(g312,g316)
    c: Coincident(g177,g182)
    c: Coincident(g176,g180)
    c: Coincident(g49,g54)
    c: Coincident(g48,g52)
    c: Coincident(g729,g735)
    c: Coincident(g728,g733)
    c: Coincident(g731,g735)
    c: Coincident(g731,g733)
    c: Coincident(g593,g599)
    c: Coincident(g592,g597)
    c: Coincident(g465,g471)
    c: Coincident(g464,g469)
    c: Coincident(g313,g319)
    c: Coincident(g312,g317)
    c: Coincident(g177,g183)
    c: Coincident(g176,g181)
    c: Coincident(g49,g55)
    c: Coincident(g48,g53)
    c: Coincident(g595,g599)
    c: Coincident(g595,g597)
    c: Coincident(g467,g471)
    c: Coincident(g467,g469)
    c: Coincident(g315,g319)
    c: Coincident(g315,g317)
    c: Coincident(g179,g183)
    c: Coincident(g179,g181)
    c: Coincident(g51,g55)
    c: Coincident(g51,g53)
    c: Coincident(g602,g606)
    c: Coincident(g602,g604)
    c: Coincident(g474,g478)
    c: Coincident(g474,g476)
    c: Coincident(g322,g326)
    c: Coincident(g322,g324)
    c: Coincident(g186,g190)
    c: Coincident(g186,g188)
    c: Coincident(g58,g62)
    c: Coincident(g58,g60)
    c: Coincident(g601,g606)
    c: Coincident(g600,g604)
    c: Coincident(g473,g478)
    c: Coincident(g472,g476)
    c: Coincident(g321,g326)
    c: Coincident(g320,g324)
    c: Coincident(g185,g190)
    c: Coincident(g184,g188)
    c: Coincident(g57,g62)
    c: Coincident(g56,g60)
    c: Coincident(g746,g750)
    c: Coincident(g746,g748)
    c: Coincident(g745,g750)
    c: Coincident(g744,g748)
    c: Coincident(g745,g751)
    c: Coincident(g744,g749)
    c: Coincident(g747,g751)
    c: Coincident(g747,g749)
    c: Coincident(g601,g607)
    c: Coincident(g600,g605)
    c: Coincident(g473,g479)
    c: Coincident(g472,g477)
    c: Coincident(g321,g327)
    c: Coincident(g320,g325)
    c: Coincident(g185,g191)
    c: Coincident(g184,g189)
    c: Coincident(g57,g63)
    c: Coincident(g56,g61)
    c: Coincident(g603,g607)
    c: Coincident(g603,g605)
    c: Coincident(g475,g479)
    c: Coincident(g475,g477)
    c: Coincident(g323,g327)
    c: Coincident(g323,g325)
    c: Coincident(g187,g191)
    c: Coincident(g187,g189)
    c: Coincident(g59,g63)
    c: Coincident(g59,g61)
    c: Coincident(g738,g742)
    c: Coincident(g738,g740)
    c: Coincident(g610,g614)
    c: Coincident(g610,g612)
    c: Coincident(g482,g486)
    c: Coincident(g482,g484)
    c: Coincident(g330,g334)
    c: Coincident(g330,g332)
    c: Coincident(g194,g198)
    c: Coincident(g194,g196)
    c: Coincident(g66,g70)
    c: Coincident(g66,g68)
    c: Coincident(g737,g742)
    c: Coincident(g736,g740)
    c: Coincident(g609,g614)
    c: Coincident(g608,g612)
    c: Coincident(g481,g486)
    c: Coincident(g480,g484)
    c: Coincident(g329,g334)
    c: Coincident(g328,g332)
    c: Coincident(g193,g198)
    c: Coincident(g192,g196)
    c: Coincident(g65,g70)
    c: Coincident(g64,g68)
    c: Coincident(g737,g743)
    c: Coincident(g736,g741)
    c: Coincident(g609,g615)
    c: Coincident(g608,g613)
    c: Coincident(g481,g487)
    c: Coincident(g480,g485)
    c: Coincident(g329,g335)
    c: Coincident(g328,g333)
    c: Coincident(g193,g199)
    c: Coincident(g192,g197)
    c: Coincident(g65,g71)
    c: Coincident(g64,g69)
    c: Coincident(g739,g743)
    c: Coincident(g739,g741)
    c: Coincident(g611,g615)
    c: Coincident(g611,g613)
    c: Coincident(g483,g487)
    c: Coincident(g483,g485)
    c: Coincident(g331,g335)
    c: Coincident(g331,g333)
    c: Coincident(g195,g199)
    c: Coincident(g195,g197)
    c: Coincident(g67,g71)
    c: Coincident(g67,g69)
    c: Coincident(g618,g622)
    c: Coincident(g618,g620)
    c: Coincident(g490,g494)
    c: Coincident(g490,g492)
    c: Coincident(g338,g342)
    c: Coincident(g338,g340)
    c: Coincident(g202,g206)
    c: Coincident(g202,g204)
    c: Coincident(g74,g78)
    c: Coincident(g74,g76)
    c: Coincident(g617,g622)
    c: Coincident(g616,g620)
    c: Coincident(g489,g494)
    c: Coincident(g488,g492)
    c: Coincident(g337,g342)
    c: Coincident(g336,g340)
    c: Coincident(g201,g206)
    c: Coincident(g200,g204)
    c: Coincident(g73,g78)
    c: Coincident(g72,g76)
    c: Coincident(g754,g758)
    c: Coincident(g754,g756)
    c: Coincident(g753,g758)
    c: Coincident(g752,g756)
    c: Coincident(g753,g759)
    c: Coincident(g752,g757)
    c: Coincident(g755,g759)
    c: Coincident(g755,g757)
    c: Coincident(g617,g623)
    c: Coincident(g616,g621)
    c: Coincident(g489,g495)
    c: Coincident(g488,g493)
    c: Coincident(g337,g343)
    c: Coincident(g336,g341)
    c: Coincident(g201,g207)
    c: Coincident(g200,g205)
    c: Coincident(g73,g79)
    c: Coincident(g72,g77)
    c: Coincident(g619,g623)
    c: Coincident(g619,g621)
    c: Coincident(g491,g495)
    c: Coincident(g491,g493)
    c: Coincident(g339,g343)
    c: Coincident(g339,g341)
    c: Coincident(g203,g207)
    c: Coincident(g203,g205)
    c: Coincident(g75,g79)
    c: Coincident(g75,g77)
    c: Coincident(g762,g766)
    c: Coincident(g762,g764)
    c: Coincident(g626,g630)
    c: Coincident(g626,g628)
    c: Coincident(g498,g502)
    c: Coincident(g498,g500)
    c: Coincident(g346,g350)
    c: Coincident(g346,g348)
    c: Coincident(g210,g214)
    c: Coincident(g210,g212)
    c: Coincident(g82,g86)
    c: Coincident(g82,g84)
    c: Coincident(g761,g766)
    c: Coincident(g760,g764)
    c: Coincident(g625,g630)
    c: Coincident(g624,g628)
    c: Coincident(g497,g502)
    c: Coincident(g496,g500)
    c: Coincident(g345,g350)
    c: Coincident(g344,g348)
    c: Coincident(g209,g214)
    c: Coincident(g208,g212)
    c: Coincident(g81,g86)
    c: Coincident(g80,g84)
    c: Coincident(g761,g767)
    c: Coincident(g760,g765)
    c: Coincident(g625,g631)
    c: Coincident(g624,g629)
    c: Coincident(g497,g503)
    c: Coincident(g496,g501)
    c: Coincident(g345,g351)
    c: Coincident(g344,g349)
    c: Coincident(g209,g215)
    c: Coincident(g208,g213)
    c: Coincident(g81,g87)
    c: Coincident(g80,g85)
    c: Coincident(g763,g767)
    c: Coincident(g763,g765)
    c: Coincident(g627,g631)
    c: Coincident(g627,g629)
    c: Coincident(g499,g503)
    c: Coincident(g499,g501)
    c: Coincident(g347,g351)
    c: Coincident(g347,g349)
    c: Coincident(g211,g215)
    c: Coincident(g211,g213)
    c: Coincident(g83,g87)
    c: Coincident(g83,g85)
    c: Coincident(g770,g774)
    c: Coincident(g770,g772)
    c: Coincident(g634,g638)
    c: Coincident(g634,g636)
    c: Coincident(g506,g510)
    c: Coincident(g506,g508)
    c: Coincident(g354,g358)
    c: Coincident(g354,g356)
    c: Coincident(g218,g222)
    c: Coincident(g218,g220)
    c: Coincident(g90,g94)
    c: Coincident(g90,g92)
    c: Coincident(g769,g774)
    c: Coincident(g768,g772)
    c: Coincident(g633,g638)
    c: Coincident(g632,g636)
    c: Coincident(g505,g510)
    c: Coincident(g504,g508)
    c: Coincident(g353,g358)
    c: Coincident(g352,g356)
    c: Coincident(g217,g222)
    c: Coincident(g216,g220)
    c: Coincident(g89,g94)
    c: Coincident(g88,g92)
    c: Coincident(g769,g775)
    c: Coincident(g768,g773)
    c: Coincident(g633,g639)
    c: Coincident(g632,g637)
    c: Coincident(g505,g511)
    c: Coincident(g504,g509)
    c: Coincident(g353,g359)
    c: Coincident(g352,g357)
    c: Coincident(g217,g223)
    c: Coincident(g216,g221)
    c: Coincident(g89,g95)
    c: Coincident(g88,g93)
    c: Coincident(g771,g775)
    c: Coincident(g771,g773)
    c: Coincident(g635,g639)
    c: Coincident(g635,g637)
    c: Coincident(g507,g511)
    c: Coincident(g507,g509)
    c: Coincident(g355,g359)
    c: Coincident(g355,g357)
    c: Coincident(g219,g223)
    c: Coincident(g219,g221)
    c: Coincident(g91,g95)
    c: Coincident(g91,g93)
    c: Coincident(g778,g782)
    c: Coincident(g778,g780)
    c: Coincident(g642,g646)
    c: Coincident(g642,g644)
    c: Coincident(g514,g518)
    c: Coincident(g514,g516)
    c: Coincident(g362,g366)
    c: Coincident(g362,g364)
    c: Coincident(g226,g230)
    c: Coincident(g226,g228)
    c: Coincident(g98,g102)
    c: Coincident(g98,g100)
    c: Coincident(g777,g782)
    c: Coincident(g776,g780)
    c: Coincident(g641,g646)
    c: Coincident(g640,g644)
    c: Coincident(g513,g518)
    c: Coincident(g512,g516)
    c: Coincident(g361,g366)
    c: Coincident(g360,g364)
    c: Coincident(g225,g230)
    c: Coincident(g224,g228)
    c: Coincident(g97,g102)
    c: Coincident(g96,g100)
    c: Coincident(g777,g783)
    c: Coincident(g776,g781)
    c: Coincident(g641,g647)
    c: Coincident(g640,g645)
    c: Coincident(g513,g519)
    c: Coincident(g512,g517)
    c: Coincident(g361,g367)
    c: Coincident(g360,g365)
    c: Coincident(g225,g231)
    c: Coincident(g224,g229)
    c: Coincident(g97,g103)
    c: Coincident(g96,g101)
    c: Coincident(g779,g783)
    c: Coincident(g779,g781)
    c: Coincident(g643,g647)
    c: Coincident(g643,g645)
    c: Coincident(g515,g519)
    c: Coincident(g515,g517)
    c: Coincident(g363,g367)
    c: Coincident(g363,g365)
    c: Coincident(g227,g231)
    c: Coincident(g227,g229)
    c: Coincident(g99,g103)
    c: Coincident(g99,g101)
    c: Coincident(g385,g391)
    c: Coincident(g385,g390)
    c: Coincident(g377,g383)
    c: Coincident(g377,g382)
    c: Coincident(g387,g391)
    c: Coincident(g386,g390)
    c: Coincident(g379,g383)
    c: Coincident(g378,g382)
    c: Coincident(g786,g790)
    c: Coincident(g786,g788)
    c: Coincident(g650,g654)
    c: Coincident(g650,g652)
    c: Coincident(g369,g375)
    c: Coincident(g369,g374)
    c: Coincident(g234,g238)
    c: Coincident(g234,g236)
    c: Coincident(g785,g790)
    c: Coincident(g784,g788)
    c: Coincident(g649,g654)
    c: Coincident(g648,g652)
    c: Coincident(g371,g375)
    c: Coincident(g370,g374)
    c: Coincident(g233,g238)
    c: Coincident(g232,g236)
    c: Coincident(g387,g389)
    c: Coincident(g386,g388)
    c: Coincident(g379,g381)
    c: Coincident(g378,g380)
    c: Coincident(g384,g389)
    c: Coincident(g384,g388)
    c: Coincident(g376,g381)
    c: Coincident(g376,g380)
    c: Coincident(g785,g791)
    c: Coincident(g784,g789)
    c: Coincident(g649,g655)
    c: Coincident(g648,g653)
    c: Coincident(g371,g373)
    c: Coincident(g370,g372)
    c: Coincident(g233,g239)
    c: Coincident(g232,g237)
    c: Coincident(g787,g791)
    c: Coincident(g787,g789)
    c: Coincident(g651,g655)
    c: Coincident(g651,g653)
    c: Coincident(g368,g373)
    c: Coincident(g368,g372)
    c: Coincident(g235,g239)
    c: Coincident(g235,g237)
    c: Coincident(g794,g798)
    c: Coincident(g794,g796)
    c: Coincident(g658,g662)
    c: Coincident(g658,g660)
    c: Coincident(g522,g526)
    c: Coincident(g522,g524)
    c: Coincident(g394,g398)
    c: Coincident(g394,g396)
    c: Coincident(g242,g246)
    c: Coincident(g242,g244)
    c: Coincident(g106,g110)
    c: Coincident(g106,g108)
    c: Coincident(g793,g798)
    c: Coincident(g792,g796)
    c: Coincident(g657,g662)
    c: Coincident(g656,g660)
    c: Coincident(g521,g526)
    c: Coincident(g520,g524)
    c: Coincident(g393,g398)
    c: Coincident(g392,g396)
    c: Coincident(g241,g246)
    c: Coincident(g240,g244)
    c: Coincident(g105,g110)
    c: Coincident(g104,g108)
    c: Coincident(g793,g799)
    c: Coincident(g792,g797)
    c: Coincident(g657,g663)
    c: Coincident(g656,g661)
    c: Coincident(g521,g527)
    c: Coincident(g520,g525)
    c: Coincident(g393,g399)
    c: Coincident(g392,g397)
    c: Coincident(g241,g247)
    c: Coincident(g240,g245)
    c: Coincident(g105,g111)
    c: Coincident(g104,g109)
    c: Coincident(g795,g799)
    c: Coincident(g795,g797)
    c: Coincident(g659,g663)
    c: Coincident(g659,g661)
    c: Coincident(g523,g527)
    c: Coincident(g523,g525)
    c: Coincident(g395,g399)
    c: Coincident(g395,g397)
    c: Coincident(g243,g247)
    c: Coincident(g243,g245)
    c: Coincident(g107,g111)
    c: Coincident(g107,g109)
    c: Coincident(g802,g806)
    c: Coincident(g802,g804)
    c: Coincident(g666,g670)
    c: Coincident(g666,g668)
    c: Coincident(g530,g534)
    c: Coincident(g530,g532)
    c: Coincident(g402,g406)
    c: Coincident(g402,g404)
    c: Coincident(g250,g254)
    c: Coincident(g250,g252)
    c: Coincident(g114,g118)
    c: Coincident(g114,g116)
    c: Coincident(g801,g806)
    c: Coincident(g800,g804)
    c: Coincident(g665,g670)
    c: Coincident(g664,g668)
    c: Coincident(g529,g534)
    c: Coincident(g528,g532)
    c: Coincident(g401,g406)
    c: Coincident(g400,g404)
    c: Coincident(g249,g254)
    c: Coincident(g248,g252)
    c: Coincident(g113,g118)
    c: Coincident(g112,g116)
    c: Coincident(g801,g807)
    c: Coincident(g800,g805)
    c: Coincident(g665,g671)
    c: Coincident(g664,g669)
    c: Coincident(g529,g535)
    c: Coincident(g528,g533)
    c: Coincident(g401,g407)
    c: Coincident(g400,g405)
    c: Coincident(g249,g255)
    c: Coincident(g248,g253)
    c: Coincident(g113,g119)
    c: Coincident(g112,g117)
    c: Coincident(g803,g807)
    c: Coincident(g803,g805)
    c: Coincident(g667,g671)
    c: Coincident(g667,g669)
    c: Coincident(g531,g535)
    c: Coincident(g531,g533)
    c: Coincident(g403,g407)
    c: Coincident(g403,g405)
    c: Coincident(g251,g255)
    c: Coincident(g251,g253)
    c: Coincident(g115,g119)
    c: Coincident(g115,g117)
    c: Coincident(g810,g814)
    c: Coincident(g810,g812)
    c: Coincident(g674,g678)
    c: Coincident(g674,g676)
    c: Coincident(g538,g542)
    c: Coincident(g538,g540)
    c: Coincident(g410,g414)
    c: Coincident(g410,g412)
    c: Coincident(g258,g262)
    c: Coincident(g258,g260)
    c: Coincident(g122,g126)
    c: Coincident(g122,g124)
    c: Coincident(g809,g814)
    c: Coincident(g808,g812)
    c: Coincident(g673,g678)
    c: Coincident(g672,g676)
    c: Coincident(g537,g542)
    c: Coincident(g536,g540)
    c: Coincident(g409,g414)
    c: Coincident(g408,g412)
    c: Coincident(g257,g262)
    c: Coincident(g256,g260)
    c: Coincident(g121,g126)
    c: Coincident(g120,g124)
    c: Coincident(g809,g815)
    c: Coincident(g808,g813)
    c: Coincident(g673,g679)
    c: Coincident(g672,g677)
    c: Coincident(g537,g543)
    c: Coincident(g536,g541)
    c: Coincident(g409,g415)
    c: Coincident(g408,g413)
    c: Coincident(g257,g263)
    c: Coincident(g256,g261)
    c: Coincident(g121,g127)
    c: Coincident(g120,g125)
    c: Coincident(g811,g815)
    c: Coincident(g811,g813)
    c: Coincident(g675,g679)
    c: Coincident(g675,g677)
    c: Coincident(g539,g543)
    c: Coincident(g539,g541)
    c: Coincident(g411,g415)
    c: Coincident(g411,g413)
    c: Coincident(g259,g263)
    c: Coincident(g259,g261)
    c: Coincident(g123,g127)
    c: Coincident(g123,g125)
FEATURE [Sketcher::SketchObject] Sketch001
  ArcFitTolerance = 1e-06
  AttachmentSupport = -> [XY_Plane]
  FullyConstrained = false
  MakeInternals = false
  MapMode = 5
  sketch-geometry (10):
    g0: LineSegment StartX=-9.09122 StartY=0.343515 StartZ=0 EndX=-9.09122 EndY=-122.901 EndZ=0
    g1: LineSegment StartX=-1.04883 StartY=-130.944 StartZ=0 EndX=351.232 EndY=-130.944 EndZ=0
    g2: LineSegment StartX=359.275 StartY=-122.901 StartZ=0 EndX=359.275 EndY=0.343515 EndZ=0
    g3: LineSegment StartX=351.232 StartY=8.38591 StartZ=0 EndX=-1.04883 EndY=8.38591 EndZ=0
    g4: ArcOfCircle CenterX=-1.04883 CenterY=0.343515 CenterZ=0 NormalX=0 NormalY=0 NormalZ=1 AngleXU=0 Radius=8.04239 StartAngle=1.5708 EndAngle=3.14159
    g5: ArcOfCircle CenterX=-1.04883 CenterY=-122.901 CenterZ=0 NormalX=0 NormalY=0 NormalZ=1 AngleXU=0 Radius=8.04239 StartAngle=3.14159 EndAngle=4.71239
    g6: ArcOfCircle CenterX=351.232 CenterY=-122.901 CenterZ=0 NormalX=0 NormalY=0 NormalZ=1 AngleXU=0 Radius=8.04239 StartAngle=4.71239 EndAngle=6.28319
    g7: ArcOfCircle CenterX=351.232 CenterY=0.343515 CenterZ=0 NormalX=0 NormalY=0 NormalZ=1 AngleXU=0 Radius=8.04239 StartAngle=0 EndAngle=1.5708
    g8: GeomPoint [constr] X=-9.09122 Y=8.38591 Z=0
    g9: GeomPoint [constr] X=359.275 Y=-130.944 Z=0
  constraints (19):
    c: Tangent(g0,g4) = -1.5708
    c: Tangent(g0,g5) = -1.5708
    c: Tangent(g1,g5) = -1.5708
    c: Tangent(g1,g6) = -1.5708
    c: Tangent(g2,g6) = -1.5708
    c: Tangent(g2,g7) = -1.5708
    c: Tangent(g3,g7) = -1.5708
    c: Tangent(g3,g4) = -1.5708
    c: Vertical(g0)
    c: Vertical(g2)
    c: Horizontal(g1)
    c: Horizontal(g3)
    c: Equal(g4,g5)
    c: Equal(g5,g6)
    c: Equal(g6,g7)
    c: PointOnObject(g8,g0)
    c: PointOnObject(g8,g3)
    c: PointOnObject(g9,g1)
    c: PointOnObject(g9,g2)
FEATURE [PartDesign::Body] Body
  AllowCompound = false
  Group = -> [Sketch001]
  Origin = -> Origin
